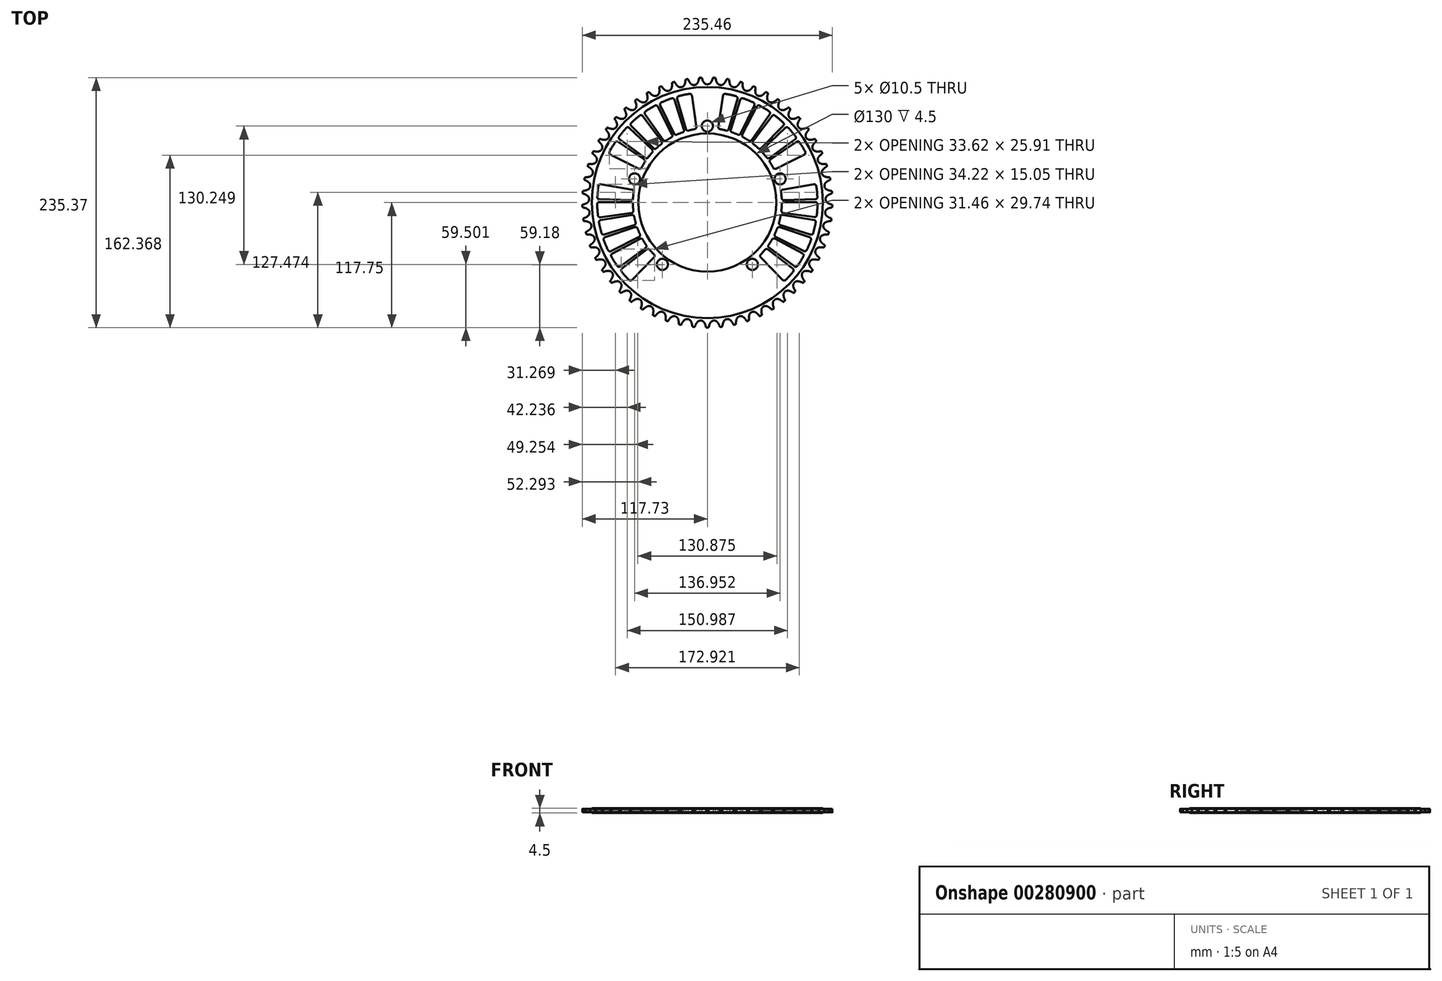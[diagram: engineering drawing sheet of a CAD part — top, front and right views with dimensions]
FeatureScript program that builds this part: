
annotation { "Feature Type Name" : "Feature", "Feature Type Description" : "" }
export const myFeature = defineFeature(function(context is Context, id is Id, definition is map)
    precondition{}
    {
        {
            var Q0;
            Q0=qCreatedBy(makeId("Top.planeOp"),FACE);
            var sketch = newSketch(context, id + "F0", { "sketchPlane" : qUnion([Q0])});
            skCircle(sketch, "E0", {"center": v(0, 0) * mm, "radius": 115.3 * mm, "construction": true});
            skArc(sketch, "E1", {"start": v(-3.25, 112.93) * mm, "mid": v(-1.82, 111.72) * mm, "end": v(0, 111.28) * mm});
            skArc(sketch, "E2", {"start": v(-4.68, 115.65) * mm, "mid": v(-4.07, 114.24) * mm, "end": v(-3.25, 112.93) * mm});
            skLineSegment(sketch, "E3", {"start": v(-4.68, 115.65) * mm, "end": v(-5.07, 116.77) * mm});
            skArc(sketch, "E4", {"start": v(-5.07, 116.77) * mm, "mid": v(-5.69, 118.06) * mm, "end": v(-6.58, 119.19) * mm});
            skArc(sketch, "E5.MirrorCS", {"start": v(3.25, 112.93) * mm, "mid": v(1.82, 111.72) * mm, "end": v(0, 111.28) * mm});
            skArc(sketch, "E6.MirrorCS", {"start": v(4.68, 115.65) * mm, "mid": v(4.07, 114.24) * mm, "end": v(3.25, 112.93) * mm});
            skArc(sketch, "E7.MirrorCS", {"start": v(5.07, 116.77) * mm, "mid": v(5.69, 118.06) * mm, "end": v(6.58, 119.19) * mm});
            skLineSegment(sketch, "E8.MirrorCS", {"start": v(4.68, 115.65) * mm, "end": v(5.07, 116.77) * mm});
            skArc(sketch, "E9.1.0", {"start": v(-17.38, 114.43) * mm, "mid": v(-16.6, 113.1) * mm, "end": v(-15.65, 111.89) * mm});
            skArc(sketch, "E9.1.1", {"start": v(-9.2, 112.6) * mm, "mid": v(-10.48, 111.24) * mm, "end": v(-12.24, 110.6) * mm});
            skArc(sketch, "E9.1.2", {"start": v(-8.07, 115.46) * mm, "mid": v(-8.53, 114) * mm, "end": v(-9.2, 112.6) * mm});
            skArc(sketch, "E9.1.3", {"start": v(-7.8, 116.62) * mm, "mid": v(-7.34, 117.97) * mm, "end": v(-6.58, 119.19) * mm});
            skArc(sketch, "E9.1.4", {"start": v(-17.88, 115.5) * mm, "mid": v(-18.64, 116.72) * mm, "end": v(-19.65, 117.74) * mm});
            skArc(sketch, "E9.1.5", {"start": v(-15.65, 111.89) * mm, "mid": v(-14.1, 110.84) * mm, "end": v(-12.24, 110.6) * mm});
            skLineSegment(sketch, "E9.1.6", {"start": v(-17.38, 114.43) * mm, "end": v(-17.88, 115.5) * mm});
            skLineSegment(sketch, "E9.1.7", {"start": v(-8.07, 115.46) * mm, "end": v(-7.8, 116.62) * mm});
            skArc(sketch, "E9.2.0", {"start": v(-29.86, 111.82) * mm, "mid": v(-28.95, 110.58) * mm, "end": v(-27.86, 109.49) * mm});
            skArc(sketch, "E9.2.1", {"start": v(-21.53, 110.9) * mm, "mid": v(-22.65, 109.41) * mm, "end": v(-24.33, 108.59) * mm});
            skArc(sketch, "E9.2.2", {"start": v(-20.72, 113.87) * mm, "mid": v(-21.01, 112.36) * mm, "end": v(-21.53, 110.9) * mm});
            skArc(sketch, "E9.2.3", {"start": v(-20.59, 115.05) * mm, "mid": v(-20.27, 116.45) * mm, "end": v(-19.65, 117.74) * mm});
            skArc(sketch, "E9.2.4", {"start": v(-30.48, 112.83) * mm, "mid": v(-31.37, 113.96) * mm, "end": v(-32.48, 114.86) * mm});
            skArc(sketch, "E9.2.5", {"start": v(-27.86, 109.49) * mm, "mid": v(-26.2, 108.61) * mm, "end": v(-24.33, 108.59) * mm});
            skLineSegment(sketch, "E9.2.6", {"start": v(-29.86, 111.82) * mm, "end": v(-30.48, 112.83) * mm});
            skLineSegment(sketch, "E9.2.7", {"start": v(-20.72, 113.87) * mm, "end": v(-20.59, 115.05) * mm});
            skArc(sketch, "E9.3.0", {"start": v(-41.98, 107.86) * mm, "mid": v(-40.94, 106.73) * mm, "end": v(-39.74, 105.76) * mm});
            skArc(sketch, "E9.3.1", {"start": v(-33.6, 107.87) * mm, "mid": v(-34.55, 106.25) * mm, "end": v(-36.13, 105.25) * mm});
            skArc(sketch, "E9.3.2", {"start": v(-33.12, 110.9) * mm, "mid": v(-33.25, 109.37) * mm, "end": v(-33.6, 107.87) * mm});
            skArc(sketch, "E9.3.3", {"start": v(-33.12, 112.09) * mm, "mid": v(-32.96, 113.51) * mm, "end": v(-32.48, 114.86) * mm});
            skArc(sketch, "E9.3.4", {"start": v(-42.7, 108.8) * mm, "mid": v(-43.71, 109.82) * mm, "end": v(-44.92, 110.6) * mm});
            skArc(sketch, "E9.3.5", {"start": v(-39.74, 105.76) * mm, "mid": v(-38, 105.07) * mm, "end": v(-36.13, 105.25) * mm});
            skLineSegment(sketch, "E9.3.6", {"start": v(-41.98, 107.86) * mm, "end": v(-42.7, 108.8) * mm});
            skLineSegment(sketch, "E9.3.7", {"start": v(-33.12, 110.9) * mm, "end": v(-33.12, 112.09) * mm});
            skArc(sketch, "E9.4.0", {"start": v(-53.6, 102.59) * mm, "mid": v(-52.43, 101.58) * mm, "end": v(-51.13, 100.75) * mm});
            skArc(sketch, "E9.4.1", {"start": v(-45.26, 103.52) * mm, "mid": v(-46.03, 101.8) * mm, "end": v(-47.5, 100.64) * mm});
            skArc(sketch, "E9.4.2", {"start": v(-45.12, 106.59) * mm, "mid": v(-45.08, 105.05) * mm, "end": v(-45.26, 103.52) * mm});
            skArc(sketch, "E9.4.3", {"start": v(-45.25, 107.76) * mm, "mid": v(-45.24, 109.2) * mm, "end": v(-44.92, 110.6) * mm});
            skArc(sketch, "E9.4.4", {"start": v(-54.42, 103.44) * mm, "mid": v(-55.53, 104.34) * mm, "end": v(-56.81, 104.98) * mm});
            skArc(sketch, "E9.4.5", {"start": v(-51.13, 100.75) * mm, "mid": v(-49.32, 100.25) * mm, "end": v(-47.5, 100.64) * mm});
            skLineSegment(sketch, "E9.4.6", {"start": v(-53.6, 102.59) * mm, "end": v(-54.42, 103.44) * mm});
            skLineSegment(sketch, "E9.4.7", {"start": v(-45.12, 106.59) * mm, "end": v(-45.25, 107.76) * mm});
            skArc(sketch, "E9.5.0", {"start": v(-64.55, 96.07) * mm, "mid": v(-63.29, 95.2) * mm, "end": v(-61.9, 94.5) * mm});
            skArc(sketch, "E9.5.1", {"start": v(-56.37, 97.9) * mm, "mid": v(-56.95, 96.13) * mm, "end": v(-58.27, 94.8) * mm});
            skArc(sketch, "E9.5.2", {"start": v(-56.57, 100.98) * mm, "mid": v(-56.36, 99.45) * mm, "end": v(-56.37, 97.9) * mm});
            skArc(sketch, "E9.5.3", {"start": v(-56.83, 102.13) * mm, "mid": v(-56.98, 103.56) * mm, "end": v(-56.81, 104.98) * mm});
            skArc(sketch, "E9.5.4", {"start": v(-65.47, 96.82) * mm, "mid": v(-66.67, 97.6) * mm, "end": v(-68.02, 98.1) * mm});
            skArc(sketch, "E9.5.5", {"start": v(-61.9, 94.5) * mm, "mid": v(-60.05, 94.22) * mm, "end": v(-58.27, 94.8) * mm});
            skLineSegment(sketch, "E9.5.6", {"start": v(-64.55, 96.07) * mm, "end": v(-65.47, 96.82) * mm});
            skLineSegment(sketch, "E9.5.7", {"start": v(-56.57, 100.98) * mm, "end": v(-56.83, 102.13) * mm});
            skArc(sketch, "E9.6.0", {"start": v(-74.73, 88.39) * mm, "mid": v(-73.37, 87.65) * mm, "end": v(-71.93, 87.13) * mm});
            skArc(sketch, "E9.6.1", {"start": v(-66.8, 91.11) * mm, "mid": v(-67.18, 89.28) * mm, "end": v(-68.35, 87.82) * mm});
            skArc(sketch, "E9.6.2", {"start": v(-67.34, 94.14) * mm, "mid": v(-66.96, 92.65) * mm, "end": v(-66.8, 91.11) * mm});
            skArc(sketch, "E9.6.3", {"start": v(-67.72, 95.26) * mm, "mid": v(-68.03, 96.66) * mm, "end": v(-68.02, 98.1) * mm});
            skArc(sketch, "E9.6.4", {"start": v(-75.72, 89.03) * mm, "mid": v(-77, 89.68) * mm, "end": v(-78.4, 90.02) * mm});
            skArc(sketch, "E9.6.5", {"start": v(-71.93, 87.13) * mm, "mid": v(-70.05, 87.04) * mm, "end": v(-68.35, 87.82) * mm});
            skLineSegment(sketch, "E9.6.6", {"start": v(-74.73, 88.39) * mm, "end": v(-75.72, 89.03) * mm});
            skLineSegment(sketch, "E9.6.7", {"start": v(-67.34, 94.14) * mm, "end": v(-67.72, 95.26) * mm});
            skArc(sketch, "E9.7.0", {"start": v(-84, 79.63) * mm, "mid": v(-82.57, 79.05) * mm, "end": v(-81.07, 78.68) * mm});
            skArc(sketch, "E9.7.1", {"start": v(-76.42, 83.21) * mm, "mid": v(-76.6, 81.35) * mm, "end": v(-77.6, 79.76) * mm});
            skArc(sketch, "E9.7.2", {"start": v(-77.28, 86.16) * mm, "mid": v(-76.74, 84.72) * mm, "end": v(-76.42, 83.21) * mm});
            skArc(sketch, "E9.7.3", {"start": v(-77.79, 87.23) * mm, "mid": v(-78.25, 88.59) * mm, "end": v(-78.4, 90.02) * mm});
            skArc(sketch, "E9.7.4", {"start": v(-85.05, 80.16) * mm, "mid": v(-86.4, 80.66) * mm, "end": v(-87.82, 80.85) * mm});
            skArc(sketch, "E9.7.5", {"start": v(-81.07, 78.68) * mm, "mid": v(-79.2, 78.8) * mm, "end": v(-77.6, 79.76) * mm});
            skLineSegment(sketch, "E9.7.6", {"start": v(-84, 79.63) * mm, "end": v(-85.05, 80.16) * mm});
            skLineSegment(sketch, "E9.7.7", {"start": v(-77.28, 86.16) * mm, "end": v(-77.79, 87.23) * mm});
            skArc(sketch, "E9.8.0", {"start": v(-92.25, 69.9) * mm, "mid": v(-90.77, 69.48) * mm, "end": v(-89.24, 69.29) * mm});
            skArc(sketch, "E9.8.1", {"start": v(-85.11, 74.3) * mm, "mid": v(-85.08, 72.43) * mm, "end": v(-85.9, 70.74) * mm});
            skArc(sketch, "E9.8.2", {"start": v(-86.3, 77.14) * mm, "mid": v(-85.6, 75.76) * mm, "end": v(-85.11, 74.3) * mm});
            skArc(sketch, "E9.8.3", {"start": v(-86.91, 78.14) * mm, "mid": v(-87.52, 79.44) * mm, "end": v(-87.82, 80.85) * mm});
            skArc(sketch, "E9.8.4", {"start": v(-93.36, 70.32) * mm, "mid": v(-94.75, 70.67) * mm, "end": v(-96.18, 70.7) * mm});
            skArc(sketch, "E9.8.5", {"start": v(-89.24, 69.29) * mm, "mid": v(-87.4, 69.61) * mm, "end": v(-85.9, 70.74) * mm});
            skLineSegment(sketch, "E9.8.6", {"start": v(-92.25, 69.9) * mm, "end": v(-93.36, 70.32) * mm});
            skLineSegment(sketch, "E9.8.7", {"start": v(-86.3, 77.14) * mm, "end": v(-86.91, 78.14) * mm});
            skArc(sketch, "E9.9.0", {"start": v(-99.38, 59.33) * mm, "mid": v(-97.86, 59.08) * mm, "end": v(-96.32, 59.05) * mm});
            skArc(sketch, "E9.9.1", {"start": v(-92.77, 64.49) * mm, "mid": v(-92.53, 62.63) * mm, "end": v(-93.16, 60.86) * mm});
            skArc(sketch, "E9.9.2", {"start": v(-94.26, 67.17) * mm, "mid": v(-93.41, 65.88) * mm, "end": v(-92.77, 64.49) * mm});
            skArc(sketch, "E9.9.3", {"start": v(-94.98, 68.1) * mm, "mid": v(-95.73, 69.33) * mm, "end": v(-96.18, 70.7) * mm});
            skArc(sketch, "E9.9.4", {"start": v(-100.53, 59.62) * mm, "mid": v(-101.95, 59.81) * mm, "end": v(-103.38, 59.68) * mm});
            skArc(sketch, "E9.9.5", {"start": v(-96.32, 59.05) * mm, "mid": v(-94.52, 59.58) * mm, "end": v(-93.16, 60.86) * mm});
            skLineSegment(sketch, "E9.9.6", {"start": v(-99.38, 59.33) * mm, "end": v(-100.53, 59.62) * mm});
            skLineSegment(sketch, "E9.9.7", {"start": v(-94.26, 67.17) * mm, "end": v(-94.98, 68.1) * mm});
            skArc(sketch, "E9.10.0", {"start": v(-105.3, 48.04) * mm, "mid": v(-103.76, 47.95) * mm, "end": v(-102.23, 48.1) * mm});
            skArc(sketch, "E9.10.1", {"start": v(-99.3, 53.89) * mm, "mid": v(-98.86, 52.07) * mm, "end": v(-99.29, 50.25) * mm});
            skArc(sketch, "E9.10.2", {"start": v(-101.07, 56.4) * mm, "mid": v(-100.1, 55.2) * mm, "end": v(-99.3, 53.89) * mm});
            skArc(sketch, "E9.10.3", {"start": v(-101.9, 57.25) * mm, "mid": v(-102.77, 58.38) * mm, "end": v(-103.38, 59.68) * mm});
            skArc(sketch, "E9.10.4", {"start": v(-106.47, 48.2) * mm, "mid": v(-107.9, 48.24) * mm, "end": v(-109.31, 47.95) * mm});
            skArc(sketch, "E9.10.5", {"start": v(-102.23, 48.1) * mm, "mid": v(-100.5, 48.82) * mm, "end": v(-99.29, 50.25) * mm});
            skLineSegment(sketch, "E9.10.6", {"start": v(-105.3, 48.04) * mm, "end": v(-106.47, 48.2) * mm});
            skLineSegment(sketch, "E9.10.7", {"start": v(-101.07, 56.4) * mm, "end": v(-101.9, 57.25) * mm});
            skArc(sketch, "E9.11.0", {"start": v(-109.95, 36.16) * mm, "mid": v(-108.4, 36.25) * mm, "end": v(-106.9, 36.56) * mm});
            skArc(sketch, "E9.11.1", {"start": v(-104.62, 42.64) * mm, "mid": v(-103.98, 40.88) * mm, "end": v(-104.21, 39.02) * mm});
            skArc(sketch, "E9.11.2", {"start": v(-106.66, 44.94) * mm, "mid": v(-105.56, 43.86) * mm, "end": v(-104.62, 42.64) * mm});
            skArc(sketch, "E9.11.3", {"start": v(-107.58, 45.69) * mm, "mid": v(-108.57, 46.72) * mm, "end": v(-109.31, 47.95) * mm});
            skArc(sketch, "E9.11.4", {"start": v(-111.13, 36.2) * mm, "mid": v(-112.56, 36.07) * mm, "end": v(-113.93, 35.63) * mm});
            skArc(sketch, "E9.11.5", {"start": v(-106.9, 36.56) * mm, "mid": v(-105.26, 37.47) * mm, "end": v(-104.21, 39.02) * mm});
            skLineSegment(sketch, "E9.11.6", {"start": v(-109.95, 36.16) * mm, "end": v(-111.13, 36.2) * mm});
            skLineSegment(sketch, "E9.11.7", {"start": v(-106.66, 44.94) * mm, "end": v(-107.58, 45.69) * mm});
            skArc(sketch, "E9.12.0", {"start": v(-113.26, 23.85) * mm, "mid": v(-111.74, 24.1) * mm, "end": v(-110.27, 24.58) * mm});
            skArc(sketch, "E9.12.1", {"start": v(-108.68, 30.87) * mm, "mid": v(-107.85, 29.2) * mm, "end": v(-107.87, 27.32) * mm});
            skArc(sketch, "E9.12.2", {"start": v(-110.96, 32.93) * mm, "mid": v(-109.74, 31.98) * mm, "end": v(-108.68, 30.87) * mm});
            skArc(sketch, "E9.12.3", {"start": v(-111.95, 33.58) * mm, "mid": v(-113.05, 34.5) * mm, "end": v(-113.93, 35.63) * mm});
            skArc(sketch, "E9.12.4", {"start": v(-114.44, 23.75) * mm, "mid": v(-115.84, 23.47) * mm, "end": v(-117.15, 22.88) * mm});
            skArc(sketch, "E9.12.5", {"start": v(-110.27, 24.58) * mm, "mid": v(-108.74, 25.66) * mm, "end": v(-107.87, 27.32) * mm});
            skLineSegment(sketch, "E9.12.6", {"start": v(-113.26, 23.85) * mm, "end": v(-114.44, 23.75) * mm});
            skLineSegment(sketch, "E9.12.7", {"start": v(-110.96, 32.93) * mm, "end": v(-111.95, 33.58) * mm});
            skArc(sketch, "E9.13.0", {"start": v(-115.2, 11.25) * mm, "mid": v(-113.71, 11.66) * mm, "end": v(-112.3, 12.3) * mm});
            skArc(sketch, "E9.13.1", {"start": v(-111.42, 18.73) * mm, "mid": v(-110.4, 17.15) * mm, "end": v(-110.22, 15.28) * mm});
            skArc(sketch, "E9.13.2", {"start": v(-113.9, 20.52) * mm, "mid": v(-112.6, 19.72) * mm, "end": v(-111.42, 18.73) * mm});
            skArc(sketch, "E9.13.3", {"start": v(-114.96, 21.06) * mm, "mid": v(-116.16, 21.85) * mm, "end": v(-117.15, 22.88) * mm});
            skArc(sketch, "E9.13.4", {"start": v(-116.36, 11.02) * mm, "mid": v(-117.72, 10.58) * mm, "end": v(-118.96, 9.86) * mm});
            skArc(sketch, "E9.13.5", {"start": v(-112.3, 12.3) * mm, "mid": v(-110.9, 13.54) * mm, "end": v(-110.22, 15.28) * mm});
            skLineSegment(sketch, "E9.13.6", {"start": v(-115.2, 11.25) * mm, "end": v(-116.36, 11.02) * mm});
            skLineSegment(sketch, "E9.13.7", {"start": v(-113.9, 20.52) * mm, "end": v(-114.96, 21.06) * mm});
            skArc(sketch, "E9.14.0", {"start": v(-115.73, -1.5) * mm, "mid": v(-114.3, -0.92) * mm, "end": v(-112.98, -0.13) * mm});
            skArc(sketch, "E9.14.1", {"start": v(-112.8, 6.36) * mm, "mid": v(-111.62, 4.9) * mm, "end": v(-111.24, 3.07) * mm});
            skArc(sketch, "E9.14.2", {"start": v(-115.48, 7.87) * mm, "mid": v(-114.08, 7.21) * mm, "end": v(-112.8, 6.36) * mm});
            skArc(sketch, "E9.14.3", {"start": v(-116.58, 8.28) * mm, "mid": v(-117.86, 8.94) * mm, "end": v(-118.96, 9.86) * mm});
            skArc(sketch, "E9.14.4", {"start": v(-116.86, -1.85) * mm, "mid": v(-118.17, -2.43) * mm, "end": v(-119.32, -3.29) * mm});
            skArc(sketch, "E9.14.5", {"start": v(-112.98, -0.13) * mm, "mid": v(-111.72, 1.26) * mm, "end": v(-111.24, 3.07) * mm});
            skLineSegment(sketch, "E9.14.6", {"start": v(-115.73, -1.5) * mm, "end": v(-116.86, -1.85) * mm});
            skLineSegment(sketch, "E9.14.7", {"start": v(-115.48, 7.87) * mm, "end": v(-116.58, 8.28) * mm});
            skArc(sketch, "E9.15.0", {"start": v(-114.87, -14.22) * mm, "mid": v(-113.51, -13.49) * mm, "end": v(-112.28, -12.56) * mm});
            skArc(sketch, "E9.15.1", {"start": v(-112.81, -6.1) * mm, "mid": v(-111.49, -7.41) * mm, "end": v(-110.9, -9.19) * mm});
            skArc(sketch, "E9.15.2", {"start": v(-115.64, -4.88) * mm, "mid": v(-114.18, -5.38) * mm, "end": v(-112.81, -6.1) * mm});
            skArc(sketch, "E9.15.3", {"start": v(-116.79, -4.6) * mm, "mid": v(-118.13, -4.08) * mm, "end": v(-119.32, -3.29) * mm});
            skArc(sketch, "E9.15.4", {"start": v(-115.95, -14.7) * mm, "mid": v(-117.19, -15.42) * mm, "end": v(-118.24, -16.4) * mm});
            skArc(sketch, "E9.15.5", {"start": v(-112.28, -12.56) * mm, "mid": v(-111.18, -11.04) * mm, "end": v(-110.9, -9.19) * mm});
            skLineSegment(sketch, "E9.15.6", {"start": v(-114.87, -14.22) * mm, "end": v(-115.95, -14.7) * mm});
            skLineSegment(sketch, "E9.15.7", {"start": v(-115.64, -4.88) * mm, "end": v(-116.79, -4.6) * mm});
            skArc(sketch, "E9.16.0", {"start": v(-112.6, -26.77) * mm, "mid": v(-111.34, -25.9) * mm, "end": v(-110.21, -24.84) * mm});
            skArc(sketch, "E9.16.1", {"start": v(-111.46, -18.46) * mm, "mid": v(-110, -19.63) * mm, "end": v(-109.22, -21.33) * mm});
            skArc(sketch, "E9.16.2", {"start": v(-114.4, -17.57) * mm, "mid": v(-112.9, -17.91) * mm, "end": v(-111.46, -18.46) * mm});
            skArc(sketch, "E9.16.3", {"start": v(-115.57, -17.41) * mm, "mid": v(-116.96, -17.05) * mm, "end": v(-118.24, -16.4) * mm});
            skArc(sketch, "E9.16.4", {"start": v(-113.63, -27.36) * mm, "mid": v(-114.78, -28.21) * mm, "end": v(-115.72, -29.3) * mm});
            skArc(sketch, "E9.16.5", {"start": v(-110.21, -24.84) * mm, "mid": v(-109.3, -23.2) * mm, "end": v(-109.22, -21.33) * mm});
            skLineSegment(sketch, "E9.16.6", {"start": v(-112.6, -26.77) * mm, "end": v(-113.63, -27.36) * mm});
            skLineSegment(sketch, "E9.16.7", {"start": v(-114.4, -17.57) * mm, "end": v(-115.57, -17.41) * mm});
            skArc(sketch, "E9.17.0", {"start": v(-108.98, -39) * mm, "mid": v(-107.81, -37.98) * mm, "end": v(-106.81, -36.8) * mm});
            skArc(sketch, "E9.17.1", {"start": v(-108.75, -30.61) * mm, "mid": v(-107.17, -31.61) * mm, "end": v(-106.2, -33.22) * mm});
            skArc(sketch, "E9.17.2", {"start": v(-111.77, -30.05) * mm, "mid": v(-110.24, -30.22) * mm, "end": v(-108.75, -30.61) * mm});
            skArc(sketch, "E9.17.3", {"start": v(-112.96, -30.02) * mm, "mid": v(-114.38, -29.82) * mm, "end": v(-115.72, -29.3) * mm});
            skArc(sketch, "E9.17.4", {"start": v(-109.93, -39.7) * mm, "mid": v(-110.98, -40.67) * mm, "end": v(-111.79, -41.85) * mm});
            skArc(sketch, "E9.17.5", {"start": v(-106.81, -36.8) * mm, "mid": v(-106.08, -35.09) * mm, "end": v(-106.2, -33.22) * mm});
            skLineSegment(sketch, "E9.17.6", {"start": v(-108.98, -39) * mm, "end": v(-109.93, -39.7) * mm});
            skLineSegment(sketch, "E9.17.7", {"start": v(-111.77, -30.05) * mm, "end": v(-112.96, -30.02) * mm});
            skArc(sketch, "E9.18.0", {"start": v(-104.03, -50.74) * mm, "mid": v(-102.98, -49.61) * mm, "end": v(-102.12, -48.34) * mm});
            skArc(sketch, "E9.18.1", {"start": v(-104.72, -42.4) * mm, "mid": v(-103.04, -43.2) * mm, "end": v(-101.9, -44.7) * mm});
            skArc(sketch, "E9.18.2", {"start": v(-107.79, -42.17) * mm, "mid": v(-106.25, -42.17) * mm, "end": v(-104.72, -42.4) * mm});
            skArc(sketch, "E9.18.3", {"start": v(-108.97, -42.26) * mm, "mid": v(-110.4, -42.22) * mm, "end": v(-111.79, -41.85) * mm});
            skArc(sketch, "E9.18.4", {"start": v(-104.9, -51.55) * mm, "mid": v(-105.83, -52.63) * mm, "end": v(-106.5, -53.9) * mm});
            skArc(sketch, "E9.18.5", {"start": v(-102.12, -48.34) * mm, "mid": v(-101.58, -46.54) * mm, "end": v(-101.9, -44.7) * mm});
            skLineSegment(sketch, "E9.18.6", {"start": v(-104.03, -50.74) * mm, "end": v(-104.9, -51.55) * mm});
            skLineSegment(sketch, "E9.18.7", {"start": v(-107.79, -42.17) * mm, "end": v(-108.97, -42.26) * mm});
            skArc(sketch, "E9.19.0", {"start": v(-97.81, -61.88) * mm, "mid": v(-96.9, -60.64) * mm, "end": v(-96.18, -59.28) * mm});
            skArc(sketch, "E9.19.1", {"start": v(-99.42, -53.65) * mm, "mid": v(-97.66, -54.28) * mm, "end": v(-96.37, -55.64) * mm});
            skArc(sketch, "E9.19.2", {"start": v(-102.5, -53.77) * mm, "mid": v(-100.96, -53.6) * mm, "end": v(-99.42, -53.65) * mm});
            skArc(sketch, "E9.19.3", {"start": v(-103.66, -54) * mm, "mid": v(-105.09, -54.1) * mm, "end": v(-106.5, -53.9) * mm});
            skArc(sketch, "E9.19.4", {"start": v(-98.59, -62.77) * mm, "mid": v(-99.4, -63.95) * mm, "end": v(-99.93, -65.29) * mm});
            skArc(sketch, "E9.19.5", {"start": v(-96.18, -59.28) * mm, "mid": v(-95.84, -57.44) * mm, "end": v(-96.37, -55.64) * mm});
            skLineSegment(sketch, "E9.19.6", {"start": v(-97.81, -61.88) * mm, "end": v(-98.59, -62.77) * mm});
            skLineSegment(sketch, "E9.19.7", {"start": v(-102.5, -53.77) * mm, "end": v(-103.66, -54) * mm});
            skArc(sketch, "E9.20.0", {"start": v(-90.41, -72.26) * mm, "mid": v(-89.64, -70.93) * mm, "end": v(-89.07, -69.5) * mm});
            skArc(sketch, "E9.20.1", {"start": v(-92.92, -64.27) * mm, "mid": v(-91.1, -64.7) * mm, "end": v(-89.67, -65.9) * mm});
            skArc(sketch, "E9.20.2", {"start": v(-95.96, -64.72) * mm, "mid": v(-94.46, -64.38) * mm, "end": v(-92.92, -64.27) * mm});
            skArc(sketch, "E9.20.3", {"start": v(-97.09, -65.07) * mm, "mid": v(-98.5, -65.34) * mm, "end": v(-99.93, -65.29) * mm});
            skArc(sketch, "E9.20.4", {"start": v(-91.08, -73.24) * mm, "mid": v(-91.76, -74.5) * mm, "end": v(-92.14, -75.88) * mm});
            skArc(sketch, "E9.20.5", {"start": v(-89.07, -69.5) * mm, "mid": v(-88.94, -67.63) * mm, "end": v(-89.67, -65.9) * mm});
            skLineSegment(sketch, "E9.20.6", {"start": v(-90.41, -72.26) * mm, "end": v(-91.08, -73.24) * mm});
            skLineSegment(sketch, "E9.20.7", {"start": v(-95.96, -64.72) * mm, "end": v(-97.09, -65.07) * mm});
            skArc(sketch, "E9.21.0", {"start": v(-81.91, -81.77) * mm, "mid": v(-81.3, -80.36) * mm, "end": v(-80.89, -78.87) * mm});
            skArc(sketch, "E9.21.1", {"start": v(-85.29, -74.1) * mm, "mid": v(-83.43, -74.32) * mm, "end": v(-81.87, -75.37) * mm});
            skArc(sketch, "E9.21.2", {"start": v(-88.26, -74.88) * mm, "mid": v(-86.8, -74.38) * mm, "end": v(-85.29, -74.1) * mm});
            skArc(sketch, "E9.21.3", {"start": v(-89.34, -75.35) * mm, "mid": v(-90.71, -75.78) * mm, "end": v(-92.14, -75.88) * mm});
            skArc(sketch, "E9.21.4", {"start": v(-82.48, -82.81) * mm, "mid": v(-83, -84.14) * mm, "end": v(-83.23, -85.56) * mm});
            skArc(sketch, "E9.21.5", {"start": v(-80.89, -78.87) * mm, "mid": v(-80.96, -77) * mm, "end": v(-81.87, -75.37) * mm});
            skLineSegment(sketch, "E9.21.6", {"start": v(-81.91, -81.77) * mm, "end": v(-82.48, -82.81) * mm});
            skLineSegment(sketch, "E9.21.7", {"start": v(-88.26, -74.88) * mm, "end": v(-89.34, -75.35) * mm});
            skArc(sketch, "E9.22.0", {"start": v(-72.42, -90.29) * mm, "mid": v(-71.96, -88.82) * mm, "end": v(-71.72, -87.3) * mm});
            skArc(sketch, "E9.22.1", {"start": v(-76.62, -83.03) * mm, "mid": v(-74.74, -83.05) * mm, "end": v(-73.08, -83.92) * mm});
            skArc(sketch, "E9.22.2", {"start": v(-79.48, -84.14) * mm, "mid": v(-78.1, -83.48) * mm, "end": v(-76.62, -83.03) * mm});
            skArc(sketch, "E9.22.3", {"start": v(-80.5, -84.73) * mm, "mid": v(-81.82, -85.3) * mm, "end": v(-83.23, -85.56) * mm});
            skArc(sketch, "E9.22.4", {"start": v(-72.86, -91.38) * mm, "mid": v(-73.25, -92.77) * mm, "end": v(-73.32, -94.2) * mm});
            skArc(sketch, "E9.22.5", {"start": v(-71.72, -87.3) * mm, "mid": v(-72, -85.44) * mm, "end": v(-73.08, -83.92) * mm});
            skLineSegment(sketch, "E9.22.6", {"start": v(-72.42, -90.29) * mm, "end": v(-72.86, -91.38) * mm});
            skLineSegment(sketch, "E9.22.7", {"start": v(-79.48, -84.14) * mm, "end": v(-80.5, -84.73) * mm});
            skArc(sketch, "E9.23.0", {"start": v(-62.05, -97.7) * mm, "mid": v(-61.75, -96.2) * mm, "end": v(-61.68, -94.65) * mm});
            skArc(sketch, "E9.23.1", {"start": v(-67.02, -90.95) * mm, "mid": v(-65.15, -90.77) * mm, "end": v(-63.4, -91.45) * mm});
            skArc(sketch, "E9.23.2", {"start": v(-69.75, -92.37) * mm, "mid": v(-68.43, -91.56) * mm, "end": v(-67.02, -90.95) * mm});
            skArc(sketch, "E9.23.3", {"start": v(-70.7, -93.07) * mm, "mid": v(-71.94, -93.78) * mm, "end": v(-73.32, -94.2) * mm});
            skArc(sketch, "E9.23.4", {"start": v(-62.37, -98.84) * mm, "mid": v(-62.6, -100.26) * mm, "end": v(-62.5, -101.7) * mm});
            skArc(sketch, "E9.23.5", {"start": v(-61.68, -94.65) * mm, "mid": v(-62.16, -92.84) * mm, "end": v(-63.4, -91.45) * mm});
            skLineSegment(sketch, "E9.23.6", {"start": v(-62.05, -97.7) * mm, "end": v(-62.37, -98.84) * mm});
            skLineSegment(sketch, "E9.23.7", {"start": v(-69.75, -92.37) * mm, "end": v(-70.7, -93.07) * mm});
            skArc(sketch, "E9.24.0", {"start": v(-50.92, -103.94) * mm, "mid": v(-50.8, -102.4) * mm, "end": v(-50.9, -100.87) * mm});
            skArc(sketch, "E9.24.1", {"start": v(-56.6, -97.78) * mm, "mid": v(-54.77, -97.38) * mm, "end": v(-52.96, -97.87) * mm});
            skArc(sketch, "E9.24.2", {"start": v(-59.16, -99.48) * mm, "mid": v(-57.95, -98.53) * mm, "end": v(-56.6, -97.78) * mm});
            skArc(sketch, "E9.24.3", {"start": v(-60.03, -100.28) * mm, "mid": v(-61.2, -101.13) * mm, "end": v(-62.5, -101.7) * mm});
            skArc(sketch, "E9.24.4", {"start": v(-51.12, -105.1) * mm, "mid": v(-51.2, -106.54) * mm, "end": v(-50.94, -107.95) * mm});
            skArc(sketch, "E9.24.5", {"start": v(-50.9, -100.87) * mm, "mid": v(-51.57, -99.12) * mm, "end": v(-52.96, -97.87) * mm});
            skLineSegment(sketch, "E9.24.6", {"start": v(-50.92, -103.94) * mm, "end": v(-51.12, -105.1) * mm});
            skLineSegment(sketch, "E9.24.7", {"start": v(-59.16, -99.48) * mm, "end": v(-60.03, -100.28) * mm});
            skArc(sketch, "E9.25.0", {"start": v(-39.18, -108.9) * mm, "mid": v(-39.22, -107.37) * mm, "end": v(-39.49, -105.85) * mm});
            skArc(sketch, "E9.25.1", {"start": v(-45.5, -103.4) * mm, "mid": v(-43.73, -102.82) * mm, "end": v(-41.88, -103.1) * mm});
            skArc(sketch, "E9.25.2", {"start": v(-47.86, -105.39) * mm, "mid": v(-46.75, -104.3) * mm, "end": v(-45.5, -103.4) * mm});
            skArc(sketch, "E9.25.3", {"start": v(-48.64, -106.28) * mm, "mid": v(-49.7, -107.24) * mm, "end": v(-50.94, -107.95) * mm});
            skArc(sketch, "E9.25.4", {"start": v(-39.24, -110.1) * mm, "mid": v(-39.16, -111.52) * mm, "end": v(-38.76, -112.9) * mm});
            skArc(sketch, "E9.25.5", {"start": v(-39.49, -105.85) * mm, "mid": v(-40.35, -104.19) * mm, "end": v(-41.88, -103.1) * mm});
            skLineSegment(sketch, "E9.25.6", {"start": v(-39.18, -108.9) * mm, "end": v(-39.24, -110.1) * mm});
            skLineSegment(sketch, "E9.25.7", {"start": v(-47.86, -105.39) * mm, "end": v(-48.64, -106.28) * mm});
            skArc(sketch, "E9.26.0", {"start": v(-26.96, -112.56) * mm, "mid": v(-27.17, -111.03) * mm, "end": v(-27.6, -109.55) * mm});
            skArc(sketch, "E9.26.1", {"start": v(-33.85, -107.79) * mm, "mid": v(-32.15, -107) * mm, "end": v(-30.28, -107.08) * mm});
            skArc(sketch, "E9.26.2", {"start": v(-35.97, -110.01) * mm, "mid": v(-35, -108.82) * mm, "end": v(-33.85, -107.79) * mm});
            skArc(sketch, "E9.26.3", {"start": v(-36.65, -110.98) * mm, "mid": v(-37.6, -112.06) * mm, "end": v(-38.76, -112.9) * mm});
            skArc(sketch, "E9.26.4", {"start": v(-26.9, -113.74) * mm, "mid": v(-26.65, -115.15) * mm, "end": v(-26.1, -116.48) * mm});
            skArc(sketch, "E9.26.5", {"start": v(-27.6, -109.55) * mm, "mid": v(-28.65, -108) * mm, "end": v(-30.28, -107.08) * mm});
            skLineSegment(sketch, "E9.26.6", {"start": v(-26.96, -112.56) * mm, "end": v(-26.9, -113.74) * mm});
            skLineSegment(sketch, "E9.26.7", {"start": v(-35.97, -110.01) * mm, "end": v(-36.65, -110.98) * mm});
            skArc(sketch, "E9.27.0", {"start": v(-14.42, -114.84) * mm, "mid": v(-14.8, -113.35) * mm, "end": v(-15.39, -111.93) * mm});
            skArc(sketch, "E9.27.1", {"start": v(-21.79, -110.86) * mm, "mid": v(-20.18, -109.9) * mm, "end": v(-18.32, -109.76) * mm});
            skArc(sketch, "E9.27.2", {"start": v(-23.65, -113.3) * mm, "mid": v(-22.81, -112) * mm, "end": v(-21.79, -110.86) * mm});
            skArc(sketch, "E9.27.3", {"start": v(-24.22, -114.34) * mm, "mid": v(-25.04, -115.52) * mm, "end": v(-26.1, -116.48) * mm});
            skArc(sketch, "E9.27.4", {"start": v(-14.22, -116) * mm, "mid": v(-13.82, -117.39) * mm, "end": v(-13.13, -118.64) * mm});
            skArc(sketch, "E9.27.5", {"start": v(-15.39, -111.93) * mm, "mid": v(-16.6, -110.5) * mm, "end": v(-18.32, -109.76) * mm});
            skLineSegment(sketch, "E9.27.6", {"start": v(-14.42, -114.84) * mm, "end": v(-14.22, -116) * mm});
            skLineSegment(sketch, "E9.27.7", {"start": v(-23.65, -113.3) * mm, "end": v(-24.22, -114.34) * mm});
            skArc(sketch, "E9.28.0", {"start": v(-1.7, -115.73) * mm, "mid": v(-2.23, -114.29) * mm, "end": v(-2.98, -112.94) * mm});
            skArc(sketch, "E9.28.1", {"start": v(-9.46, -112.58) * mm, "mid": v(-7.97, -111.45) * mm, "end": v(-6.13, -111.11) * mm});
            skArc(sketch, "E9.28.2", {"start": v(-11.05, -115.21) * mm, "mid": v(-10.35, -113.84) * mm, "end": v(-9.46, -112.58) * mm});
            skArc(sketch, "E9.28.3", {"start": v(-11.5, -116.31) * mm, "mid": v(-12.18, -117.57) * mm, "end": v(-13.13, -118.64) * mm});
            skArc(sketch, "E9.28.4", {"start": v(-1.37, -116.87) * mm, "mid": v(-0.83, -118.2) * mm, "end": v(0, -119.37) * mm});
            skArc(sketch, "E9.28.5", {"start": v(-2.98, -112.94) * mm, "mid": v(-4.34, -111.65) * mm, "end": v(-6.13, -111.11) * mm});
            skLineSegment(sketch, "E9.28.6", {"start": v(-1.7, -115.73) * mm, "end": v(-1.37, -116.87) * mm});
            skLineSegment(sketch, "E9.28.7", {"start": v(-11.05, -115.21) * mm, "end": v(-11.5, -116.31) * mm});
            skArc(sketch, "E9.29.0", {"start": v(11.05, -115.21) * mm, "mid": v(10.35, -113.84) * mm, "end": v(9.46, -112.58) * mm});
            skArc(sketch, "E9.29.1", {"start": v(2.98, -112.94) * mm, "mid": v(4.34, -111.65) * mm, "end": v(6.13, -111.11) * mm});
            skArc(sketch, "E9.29.2", {"start": v(1.7, -115.73) * mm, "mid": v(2.23, -114.29) * mm, "end": v(2.98, -112.94) * mm});
            skArc(sketch, "E9.29.3", {"start": v(1.37, -116.87) * mm, "mid": v(0.83, -118.2) * mm, "end": v(0, -119.37) * mm});
            skArc(sketch, "E9.29.4", {"start": v(11.5, -116.31) * mm, "mid": v(12.18, -117.57) * mm, "end": v(13.13, -118.64) * mm});
            skArc(sketch, "E9.29.5", {"start": v(9.46, -112.58) * mm, "mid": v(7.97, -111.45) * mm, "end": v(6.13, -111.11) * mm});
            skLineSegment(sketch, "E9.29.6", {"start": v(11.05, -115.21) * mm, "end": v(11.5, -116.31) * mm});
            skLineSegment(sketch, "E9.29.7", {"start": v(1.7, -115.73) * mm, "end": v(1.37, -116.87) * mm});
            skArc(sketch, "E9.30.0", {"start": v(23.65, -113.3) * mm, "mid": v(22.81, -112) * mm, "end": v(21.79, -110.86) * mm});
            skArc(sketch, "E9.30.1", {"start": v(15.39, -111.93) * mm, "mid": v(16.6, -110.5) * mm, "end": v(18.32, -109.76) * mm});
            skArc(sketch, "E9.30.2", {"start": v(14.42, -114.84) * mm, "mid": v(14.8, -113.35) * mm, "end": v(15.39, -111.93) * mm});
            skArc(sketch, "E9.30.3", {"start": v(14.22, -116) * mm, "mid": v(13.82, -117.39) * mm, "end": v(13.13, -118.64) * mm});
            skArc(sketch, "E9.30.4", {"start": v(24.22, -114.34) * mm, "mid": v(25.04, -115.52) * mm, "end": v(26.1, -116.48) * mm});
            skArc(sketch, "E9.30.5", {"start": v(21.79, -110.86) * mm, "mid": v(20.18, -109.9) * mm, "end": v(18.32, -109.76) * mm});
            skLineSegment(sketch, "E9.30.6", {"start": v(23.65, -113.3) * mm, "end": v(24.22, -114.34) * mm});
            skLineSegment(sketch, "E9.30.7", {"start": v(14.42, -114.84) * mm, "end": v(14.22, -116) * mm});
            skArc(sketch, "E9.31.0", {"start": v(35.97, -110.01) * mm, "mid": v(35, -108.82) * mm, "end": v(33.85, -107.79) * mm});
            skArc(sketch, "E9.31.1", {"start": v(27.6, -109.55) * mm, "mid": v(28.65, -108) * mm, "end": v(30.28, -107.08) * mm});
            skArc(sketch, "E9.31.2", {"start": v(26.96, -112.56) * mm, "mid": v(27.17, -111.03) * mm, "end": v(27.6, -109.55) * mm});
            skArc(sketch, "E9.31.3", {"start": v(26.9, -113.74) * mm, "mid": v(26.65, -115.15) * mm, "end": v(26.1, -116.48) * mm});
            skArc(sketch, "E9.31.4", {"start": v(36.65, -110.98) * mm, "mid": v(37.6, -112.06) * mm, "end": v(38.76, -112.9) * mm});
            skArc(sketch, "E9.31.5", {"start": v(33.85, -107.79) * mm, "mid": v(32.15, -107) * mm, "end": v(30.28, -107.08) * mm});
            skLineSegment(sketch, "E9.31.6", {"start": v(35.97, -110.01) * mm, "end": v(36.65, -110.98) * mm});
            skLineSegment(sketch, "E9.31.7", {"start": v(26.96, -112.56) * mm, "end": v(26.9, -113.74) * mm});
            skArc(sketch, "E9.32.0", {"start": v(47.86, -105.39) * mm, "mid": v(46.75, -104.3) * mm, "end": v(45.5, -103.4) * mm});
            skArc(sketch, "E9.32.1", {"start": v(39.49, -105.85) * mm, "mid": v(40.35, -104.19) * mm, "end": v(41.88, -103.1) * mm});
            skArc(sketch, "E9.32.2", {"start": v(39.18, -108.9) * mm, "mid": v(39.22, -107.37) * mm, "end": v(39.49, -105.85) * mm});
            skArc(sketch, "E9.32.3", {"start": v(39.24, -110.1) * mm, "mid": v(39.16, -111.52) * mm, "end": v(38.76, -112.9) * mm});
            skArc(sketch, "E9.32.4", {"start": v(48.64, -106.28) * mm, "mid": v(49.7, -107.24) * mm, "end": v(50.94, -107.95) * mm});
            skArc(sketch, "E9.32.5", {"start": v(45.5, -103.4) * mm, "mid": v(43.73, -102.82) * mm, "end": v(41.88, -103.1) * mm});
            skLineSegment(sketch, "E9.32.6", {"start": v(47.86, -105.39) * mm, "end": v(48.64, -106.28) * mm});
            skLineSegment(sketch, "E9.32.7", {"start": v(39.18, -108.9) * mm, "end": v(39.24, -110.1) * mm});
            skArc(sketch, "E9.33.0", {"start": v(59.16, -99.48) * mm, "mid": v(57.95, -98.53) * mm, "end": v(56.6, -97.78) * mm});
            skArc(sketch, "E9.33.1", {"start": v(50.9, -100.87) * mm, "mid": v(51.57, -99.12) * mm, "end": v(52.96, -97.87) * mm});
            skArc(sketch, "E9.33.2", {"start": v(50.92, -103.94) * mm, "mid": v(50.8, -102.4) * mm, "end": v(50.9, -100.87) * mm});
            skArc(sketch, "E9.33.3", {"start": v(51.12, -105.1) * mm, "mid": v(51.2, -106.54) * mm, "end": v(50.94, -107.95) * mm});
            skArc(sketch, "E9.33.4", {"start": v(60.03, -100.28) * mm, "mid": v(61.2, -101.13) * mm, "end": v(62.5, -101.7) * mm});
            skArc(sketch, "E9.33.5", {"start": v(56.6, -97.78) * mm, "mid": v(54.77, -97.38) * mm, "end": v(52.96, -97.87) * mm});
            skLineSegment(sketch, "E9.33.6", {"start": v(59.16, -99.48) * mm, "end": v(60.03, -100.28) * mm});
            skLineSegment(sketch, "E9.33.7", {"start": v(50.92, -103.94) * mm, "end": v(51.12, -105.1) * mm});
            skArc(sketch, "E9.34.0", {"start": v(69.75, -92.37) * mm, "mid": v(68.43, -91.56) * mm, "end": v(67.02, -90.95) * mm});
            skArc(sketch, "E9.34.1", {"start": v(61.68, -94.65) * mm, "mid": v(62.16, -92.84) * mm, "end": v(63.4, -91.45) * mm});
            skArc(sketch, "E9.34.2", {"start": v(62.05, -97.7) * mm, "mid": v(61.75, -96.2) * mm, "end": v(61.68, -94.65) * mm});
            skArc(sketch, "E9.34.3", {"start": v(62.37, -98.84) * mm, "mid": v(62.6, -100.26) * mm, "end": v(62.5, -101.7) * mm});
            skArc(sketch, "E9.34.4", {"start": v(70.7, -93.07) * mm, "mid": v(71.94, -93.78) * mm, "end": v(73.32, -94.2) * mm});
            skArc(sketch, "E9.34.5", {"start": v(67.02, -90.95) * mm, "mid": v(65.15, -90.77) * mm, "end": v(63.4, -91.45) * mm});
            skLineSegment(sketch, "E9.34.6", {"start": v(69.75, -92.37) * mm, "end": v(70.7, -93.07) * mm});
            skLineSegment(sketch, "E9.34.7", {"start": v(62.05, -97.7) * mm, "end": v(62.37, -98.84) * mm});
            skArc(sketch, "E9.35.0", {"start": v(79.48, -84.14) * mm, "mid": v(78.1, -83.48) * mm, "end": v(76.62, -83.03) * mm});
            skArc(sketch, "E9.35.1", {"start": v(71.72, -87.3) * mm, "mid": v(72, -85.44) * mm, "end": v(73.08, -83.92) * mm});
            skArc(sketch, "E9.35.2", {"start": v(72.42, -90.29) * mm, "mid": v(71.96, -88.82) * mm, "end": v(71.72, -87.3) * mm});
            skArc(sketch, "E9.35.3", {"start": v(72.86, -91.38) * mm, "mid": v(73.25, -92.77) * mm, "end": v(73.32, -94.2) * mm});
            skArc(sketch, "E9.35.4", {"start": v(80.5, -84.73) * mm, "mid": v(81.82, -85.3) * mm, "end": v(83.23, -85.56) * mm});
            skArc(sketch, "E9.35.5", {"start": v(76.62, -83.03) * mm, "mid": v(74.74, -83.05) * mm, "end": v(73.08, -83.92) * mm});
            skLineSegment(sketch, "E9.35.6", {"start": v(79.48, -84.14) * mm, "end": v(80.5, -84.73) * mm});
            skLineSegment(sketch, "E9.35.7", {"start": v(72.42, -90.29) * mm, "end": v(72.86, -91.38) * mm});
            skArc(sketch, "E9.36.0", {"start": v(88.26, -74.88) * mm, "mid": v(86.8, -74.38) * mm, "end": v(85.29, -74.1) * mm});
            skArc(sketch, "E9.36.1", {"start": v(80.89, -78.87) * mm, "mid": v(80.96, -77) * mm, "end": v(81.87, -75.37) * mm});
            skArc(sketch, "E9.36.2", {"start": v(81.91, -81.77) * mm, "mid": v(81.3, -80.36) * mm, "end": v(80.89, -78.87) * mm});
            skArc(sketch, "E9.36.3", {"start": v(82.48, -82.81) * mm, "mid": v(83, -84.14) * mm, "end": v(83.23, -85.56) * mm});
            skArc(sketch, "E9.36.4", {"start": v(89.34, -75.35) * mm, "mid": v(90.71, -75.78) * mm, "end": v(92.14, -75.88) * mm});
            skArc(sketch, "E9.36.5", {"start": v(85.29, -74.1) * mm, "mid": v(83.43, -74.32) * mm, "end": v(81.87, -75.37) * mm});
            skLineSegment(sketch, "E9.36.6", {"start": v(88.26, -74.88) * mm, "end": v(89.34, -75.35) * mm});
            skLineSegment(sketch, "E9.36.7", {"start": v(81.91, -81.77) * mm, "end": v(82.48, -82.81) * mm});
            skArc(sketch, "E9.37.0", {"start": v(95.96, -64.72) * mm, "mid": v(94.46, -64.38) * mm, "end": v(92.92, -64.27) * mm});
            skArc(sketch, "E9.37.1", {"start": v(89.07, -69.5) * mm, "mid": v(88.94, -67.63) * mm, "end": v(89.67, -65.9) * mm});
            skArc(sketch, "E9.37.2", {"start": v(90.41, -72.26) * mm, "mid": v(89.64, -70.93) * mm, "end": v(89.07, -69.5) * mm});
            skArc(sketch, "E9.37.3", {"start": v(91.08, -73.24) * mm, "mid": v(91.76, -74.5) * mm, "end": v(92.14, -75.88) * mm});
            skArc(sketch, "E9.37.4", {"start": v(97.09, -65.07) * mm, "mid": v(98.5, -65.34) * mm, "end": v(99.93, -65.29) * mm});
            skArc(sketch, "E9.37.5", {"start": v(92.92, -64.27) * mm, "mid": v(91.1, -64.7) * mm, "end": v(89.67, -65.9) * mm});
            skLineSegment(sketch, "E9.37.6", {"start": v(95.96, -64.72) * mm, "end": v(97.09, -65.07) * mm});
            skLineSegment(sketch, "E9.37.7", {"start": v(90.41, -72.26) * mm, "end": v(91.08, -73.24) * mm});
            skArc(sketch, "E9.38.0", {"start": v(102.5, -53.77) * mm, "mid": v(100.96, -53.6) * mm, "end": v(99.42, -53.65) * mm});
            skArc(sketch, "E9.38.1", {"start": v(96.18, -59.28) * mm, "mid": v(95.84, -57.44) * mm, "end": v(96.37, -55.64) * mm});
            skArc(sketch, "E9.38.2", {"start": v(97.81, -61.88) * mm, "mid": v(96.9, -60.64) * mm, "end": v(96.18, -59.28) * mm});
            skArc(sketch, "E9.38.3", {"start": v(98.59, -62.77) * mm, "mid": v(99.4, -63.95) * mm, "end": v(99.93, -65.29) * mm});
            skArc(sketch, "E9.38.4", {"start": v(103.66, -54) * mm, "mid": v(105.09, -54.1) * mm, "end": v(106.5, -53.9) * mm});
            skArc(sketch, "E9.38.5", {"start": v(99.42, -53.65) * mm, "mid": v(97.66, -54.28) * mm, "end": v(96.37, -55.64) * mm});
            skLineSegment(sketch, "E9.38.6", {"start": v(102.5, -53.77) * mm, "end": v(103.66, -54) * mm});
            skLineSegment(sketch, "E9.38.7", {"start": v(97.81, -61.88) * mm, "end": v(98.59, -62.77) * mm});
            skArc(sketch, "E9.39.0", {"start": v(107.79, -42.17) * mm, "mid": v(106.25, -42.17) * mm, "end": v(104.72, -42.4) * mm});
            skArc(sketch, "E9.39.1", {"start": v(102.12, -48.34) * mm, "mid": v(101.58, -46.54) * mm, "end": v(101.9, -44.7) * mm});
            skArc(sketch, "E9.39.2", {"start": v(104.03, -50.74) * mm, "mid": v(102.98, -49.61) * mm, "end": v(102.12, -48.34) * mm});
            skArc(sketch, "E9.39.3", {"start": v(104.9, -51.55) * mm, "mid": v(105.83, -52.63) * mm, "end": v(106.5, -53.9) * mm});
            skArc(sketch, "E9.39.4", {"start": v(108.97, -42.26) * mm, "mid": v(110.4, -42.22) * mm, "end": v(111.79, -41.85) * mm});
            skArc(sketch, "E9.39.5", {"start": v(104.72, -42.4) * mm, "mid": v(103.04, -43.2) * mm, "end": v(101.9, -44.7) * mm});
            skLineSegment(sketch, "E9.39.6", {"start": v(107.79, -42.17) * mm, "end": v(108.97, -42.26) * mm});
            skLineSegment(sketch, "E9.39.7", {"start": v(104.03, -50.74) * mm, "end": v(104.9, -51.55) * mm});
            skArc(sketch, "E9.40.0", {"start": v(111.77, -30.05) * mm, "mid": v(110.24, -30.22) * mm, "end": v(108.75, -30.61) * mm});
            skArc(sketch, "E9.40.1", {"start": v(106.81, -36.8) * mm, "mid": v(106.08, -35.09) * mm, "end": v(106.2, -33.22) * mm});
            skArc(sketch, "E9.40.2", {"start": v(108.98, -39) * mm, "mid": v(107.81, -37.98) * mm, "end": v(106.81, -36.8) * mm});
            skArc(sketch, "E9.40.3", {"start": v(109.93, -39.7) * mm, "mid": v(110.98, -40.67) * mm, "end": v(111.79, -41.85) * mm});
            skArc(sketch, "E9.40.4", {"start": v(112.96, -30.02) * mm, "mid": v(114.38, -29.82) * mm, "end": v(115.72, -29.3) * mm});
            skArc(sketch, "E9.40.5", {"start": v(108.75, -30.61) * mm, "mid": v(107.17, -31.61) * mm, "end": v(106.2, -33.22) * mm});
            skLineSegment(sketch, "E9.40.6", {"start": v(111.77, -30.05) * mm, "end": v(112.96, -30.02) * mm});
            skLineSegment(sketch, "E9.40.7", {"start": v(108.98, -39) * mm, "end": v(109.93, -39.7) * mm});
            skArc(sketch, "E9.41.0", {"start": v(114.4, -17.57) * mm, "mid": v(112.9, -17.91) * mm, "end": v(111.46, -18.46) * mm});
            skArc(sketch, "E9.41.1", {"start": v(110.21, -24.84) * mm, "mid": v(109.3, -23.2) * mm, "end": v(109.22, -21.33) * mm});
            skArc(sketch, "E9.41.2", {"start": v(112.6, -26.77) * mm, "mid": v(111.34, -25.9) * mm, "end": v(110.21, -24.84) * mm});
            skArc(sketch, "E9.41.3", {"start": v(113.63, -27.36) * mm, "mid": v(114.78, -28.21) * mm, "end": v(115.72, -29.3) * mm});
            skArc(sketch, "E9.41.4", {"start": v(115.57, -17.41) * mm, "mid": v(116.96, -17.05) * mm, "end": v(118.24, -16.4) * mm});
            skArc(sketch, "E9.41.5", {"start": v(111.46, -18.46) * mm, "mid": v(110, -19.63) * mm, "end": v(109.22, -21.33) * mm});
            skLineSegment(sketch, "E9.41.6", {"start": v(114.4, -17.57) * mm, "end": v(115.57, -17.41) * mm});
            skLineSegment(sketch, "E9.41.7", {"start": v(112.6, -26.77) * mm, "end": v(113.63, -27.36) * mm});
            skArc(sketch, "E9.42.0", {"start": v(115.64, -4.88) * mm, "mid": v(114.18, -5.38) * mm, "end": v(112.81, -6.1) * mm});
            skArc(sketch, "E9.42.1", {"start": v(112.28, -12.56) * mm, "mid": v(111.18, -11.04) * mm, "end": v(110.9, -9.19) * mm});
            skArc(sketch, "E9.42.2", {"start": v(114.87, -14.22) * mm, "mid": v(113.51, -13.49) * mm, "end": v(112.28, -12.56) * mm});
            skArc(sketch, "E9.42.3", {"start": v(115.95, -14.7) * mm, "mid": v(117.19, -15.42) * mm, "end": v(118.24, -16.4) * mm});
            skArc(sketch, "E9.42.4", {"start": v(116.79, -4.6) * mm, "mid": v(118.13, -4.08) * mm, "end": v(119.32, -3.29) * mm});
            skArc(sketch, "E9.42.5", {"start": v(112.81, -6.1) * mm, "mid": v(111.49, -7.41) * mm, "end": v(110.9, -9.19) * mm});
            skLineSegment(sketch, "E9.42.6", {"start": v(115.64, -4.88) * mm, "end": v(116.79, -4.6) * mm});
            skLineSegment(sketch, "E9.42.7", {"start": v(114.87, -14.22) * mm, "end": v(115.95, -14.7) * mm});
            skArc(sketch, "E9.43.0", {"start": v(115.48, 7.87) * mm, "mid": v(114.08, 7.21) * mm, "end": v(112.8, 6.36) * mm});
            skArc(sketch, "E9.43.1", {"start": v(112.98, -0.13) * mm, "mid": v(111.72, 1.26) * mm, "end": v(111.24, 3.07) * mm});
            skArc(sketch, "E9.43.2", {"start": v(115.73, -1.5) * mm, "mid": v(114.3, -0.92) * mm, "end": v(112.98, -0.13) * mm});
            skArc(sketch, "E9.43.3", {"start": v(116.86, -1.85) * mm, "mid": v(118.17, -2.43) * mm, "end": v(119.32, -3.29) * mm});
            skArc(sketch, "E9.43.4", {"start": v(116.58, 8.28) * mm, "mid": v(117.86, 8.94) * mm, "end": v(118.96, 9.86) * mm});
            skArc(sketch, "E9.43.5", {"start": v(112.8, 6.36) * mm, "mid": v(111.62, 4.9) * mm, "end": v(111.24, 3.07) * mm});
            skLineSegment(sketch, "E9.43.6", {"start": v(115.48, 7.87) * mm, "end": v(116.58, 8.28) * mm});
            skLineSegment(sketch, "E9.43.7", {"start": v(115.73, -1.5) * mm, "end": v(116.86, -1.85) * mm});
            skArc(sketch, "E9.44.0", {"start": v(113.9, 20.52) * mm, "mid": v(112.6, 19.72) * mm, "end": v(111.42, 18.73) * mm});
            skArc(sketch, "E9.44.1", {"start": v(112.3, 12.3) * mm, "mid": v(110.9, 13.54) * mm, "end": v(110.22, 15.28) * mm});
            skArc(sketch, "E9.44.2", {"start": v(115.2, 11.25) * mm, "mid": v(113.71, 11.66) * mm, "end": v(112.3, 12.3) * mm});
            skArc(sketch, "E9.44.3", {"start": v(116.36, 11.02) * mm, "mid": v(117.72, 10.58) * mm, "end": v(118.96, 9.86) * mm});
            skArc(sketch, "E9.44.4", {"start": v(114.96, 21.06) * mm, "mid": v(116.16, 21.85) * mm, "end": v(117.15, 22.88) * mm});
            skArc(sketch, "E9.44.5", {"start": v(111.42, 18.73) * mm, "mid": v(110.4, 17.15) * mm, "end": v(110.22, 15.28) * mm});
            skLineSegment(sketch, "E9.44.6", {"start": v(113.9, 20.52) * mm, "end": v(114.96, 21.06) * mm});
            skLineSegment(sketch, "E9.44.7", {"start": v(115.2, 11.25) * mm, "end": v(116.36, 11.02) * mm});
            skArc(sketch, "E9.45.0", {"start": v(110.96, 32.93) * mm, "mid": v(109.74, 31.98) * mm, "end": v(108.68, 30.87) * mm});
            skArc(sketch, "E9.45.1", {"start": v(110.27, 24.58) * mm, "mid": v(108.74, 25.66) * mm, "end": v(107.87, 27.32) * mm});
            skArc(sketch, "E9.45.2", {"start": v(113.26, 23.85) * mm, "mid": v(111.74, 24.1) * mm, "end": v(110.27, 24.58) * mm});
            skArc(sketch, "E9.45.3", {"start": v(114.44, 23.75) * mm, "mid": v(115.84, 23.47) * mm, "end": v(117.15, 22.88) * mm});
            skArc(sketch, "E9.45.4", {"start": v(111.95, 33.58) * mm, "mid": v(113.05, 34.5) * mm, "end": v(113.93, 35.63) * mm});
            skArc(sketch, "E9.45.5", {"start": v(108.68, 30.87) * mm, "mid": v(107.85, 29.2) * mm, "end": v(107.87, 27.32) * mm});
            skLineSegment(sketch, "E9.45.6", {"start": v(110.96, 32.93) * mm, "end": v(111.95, 33.58) * mm});
            skLineSegment(sketch, "E9.45.7", {"start": v(113.26, 23.85) * mm, "end": v(114.44, 23.75) * mm});
            skArc(sketch, "E9.46.0", {"start": v(106.66, 44.94) * mm, "mid": v(105.56, 43.86) * mm, "end": v(104.62, 42.64) * mm});
            skArc(sketch, "E9.46.1", {"start": v(106.9, 36.56) * mm, "mid": v(105.26, 37.47) * mm, "end": v(104.21, 39.02) * mm});
            skArc(sketch, "E9.46.2", {"start": v(109.95, 36.16) * mm, "mid": v(108.4, 36.25) * mm, "end": v(106.9, 36.56) * mm});
            skArc(sketch, "E9.46.3", {"start": v(111.13, 36.2) * mm, "mid": v(112.56, 36.07) * mm, "end": v(113.93, 35.63) * mm});
            skArc(sketch, "E9.46.4", {"start": v(107.58, 45.69) * mm, "mid": v(108.57, 46.72) * mm, "end": v(109.31, 47.95) * mm});
            skArc(sketch, "E9.46.5", {"start": v(104.62, 42.64) * mm, "mid": v(103.98, 40.88) * mm, "end": v(104.21, 39.02) * mm});
            skLineSegment(sketch, "E9.46.6", {"start": v(106.66, 44.94) * mm, "end": v(107.58, 45.69) * mm});
            skLineSegment(sketch, "E9.46.7", {"start": v(109.95, 36.16) * mm, "end": v(111.13, 36.2) * mm});
            skArc(sketch, "E9.47.0", {"start": v(101.07, 56.4) * mm, "mid": v(100.1, 55.2) * mm, "end": v(99.3, 53.89) * mm});
            skArc(sketch, "E9.47.1", {"start": v(102.23, 48.1) * mm, "mid": v(100.5, 48.82) * mm, "end": v(99.29, 50.25) * mm});
            skArc(sketch, "E9.47.2", {"start": v(105.3, 48.04) * mm, "mid": v(103.76, 47.95) * mm, "end": v(102.23, 48.1) * mm});
            skArc(sketch, "E9.47.3", {"start": v(106.47, 48.2) * mm, "mid": v(107.9, 48.24) * mm, "end": v(109.31, 47.95) * mm});
            skArc(sketch, "E9.47.4", {"start": v(101.9, 57.25) * mm, "mid": v(102.77, 58.38) * mm, "end": v(103.38, 59.68) * mm});
            skArc(sketch, "E9.47.5", {"start": v(99.3, 53.89) * mm, "mid": v(98.86, 52.07) * mm, "end": v(99.29, 50.25) * mm});
            skLineSegment(sketch, "E9.47.6", {"start": v(101.07, 56.4) * mm, "end": v(101.9, 57.25) * mm});
            skLineSegment(sketch, "E9.47.7", {"start": v(105.3, 48.04) * mm, "end": v(106.47, 48.2) * mm});
            skArc(sketch, "E9.48.0", {"start": v(94.26, 67.17) * mm, "mid": v(93.41, 65.88) * mm, "end": v(92.77, 64.49) * mm});
            skArc(sketch, "E9.48.1", {"start": v(96.32, 59.05) * mm, "mid": v(94.52, 59.58) * mm, "end": v(93.16, 60.86) * mm});
            skArc(sketch, "E9.48.2", {"start": v(99.38, 59.33) * mm, "mid": v(97.86, 59.08) * mm, "end": v(96.32, 59.05) * mm});
            skArc(sketch, "E9.48.3", {"start": v(100.53, 59.62) * mm, "mid": v(101.95, 59.81) * mm, "end": v(103.38, 59.68) * mm});
            skArc(sketch, "E9.48.4", {"start": v(94.98, 68.1) * mm, "mid": v(95.73, 69.33) * mm, "end": v(96.18, 70.7) * mm});
            skArc(sketch, "E9.48.5", {"start": v(92.77, 64.49) * mm, "mid": v(92.53, 62.63) * mm, "end": v(93.16, 60.86) * mm});
            skLineSegment(sketch, "E9.48.6", {"start": v(94.26, 67.17) * mm, "end": v(94.98, 68.1) * mm});
            skLineSegment(sketch, "E9.48.7", {"start": v(99.38, 59.33) * mm, "end": v(100.53, 59.62) * mm});
            skArc(sketch, "E9.49.0", {"start": v(86.3, 77.14) * mm, "mid": v(85.6, 75.76) * mm, "end": v(85.11, 74.3) * mm});
            skArc(sketch, "E9.49.1", {"start": v(89.24, 69.29) * mm, "mid": v(87.4, 69.61) * mm, "end": v(85.9, 70.74) * mm});
            skArc(sketch, "E9.49.2", {"start": v(92.25, 69.9) * mm, "mid": v(90.77, 69.48) * mm, "end": v(89.24, 69.29) * mm});
            skArc(sketch, "E9.49.3", {"start": v(93.36, 70.32) * mm, "mid": v(94.75, 70.67) * mm, "end": v(96.18, 70.7) * mm});
            skArc(sketch, "E9.49.4", {"start": v(86.91, 78.14) * mm, "mid": v(87.52, 79.44) * mm, "end": v(87.82, 80.85) * mm});
            skArc(sketch, "E9.49.5", {"start": v(85.11, 74.3) * mm, "mid": v(85.08, 72.43) * mm, "end": v(85.9, 70.74) * mm});
            skLineSegment(sketch, "E9.49.6", {"start": v(86.3, 77.14) * mm, "end": v(86.91, 78.14) * mm});
            skLineSegment(sketch, "E9.49.7", {"start": v(92.25, 69.9) * mm, "end": v(93.36, 70.32) * mm});
            skArc(sketch, "E9.50.0", {"start": v(77.28, 86.16) * mm, "mid": v(76.74, 84.72) * mm, "end": v(76.42, 83.21) * mm});
            skArc(sketch, "E9.50.1", {"start": v(81.07, 78.68) * mm, "mid": v(79.2, 78.8) * mm, "end": v(77.6, 79.76) * mm});
            skArc(sketch, "E9.50.2", {"start": v(84, 79.63) * mm, "mid": v(82.57, 79.05) * mm, "end": v(81.07, 78.68) * mm});
            skArc(sketch, "E9.50.3", {"start": v(85.05, 80.16) * mm, "mid": v(86.4, 80.66) * mm, "end": v(87.82, 80.85) * mm});
            skArc(sketch, "E9.50.4", {"start": v(77.79, 87.23) * mm, "mid": v(78.25, 88.59) * mm, "end": v(78.4, 90.02) * mm});
            skArc(sketch, "E9.50.5", {"start": v(76.42, 83.21) * mm, "mid": v(76.6, 81.35) * mm, "end": v(77.6, 79.76) * mm});
            skLineSegment(sketch, "E9.50.6", {"start": v(77.28, 86.16) * mm, "end": v(77.79, 87.23) * mm});
            skLineSegment(sketch, "E9.50.7", {"start": v(84, 79.63) * mm, "end": v(85.05, 80.16) * mm});
            skArc(sketch, "E9.51.0", {"start": v(67.34, 94.14) * mm, "mid": v(66.96, 92.65) * mm, "end": v(66.8, 91.11) * mm});
            skArc(sketch, "E9.51.1", {"start": v(71.93, 87.13) * mm, "mid": v(70.05, 87.04) * mm, "end": v(68.35, 87.82) * mm});
            skArc(sketch, "E9.51.2", {"start": v(74.73, 88.39) * mm, "mid": v(73.37, 87.65) * mm, "end": v(71.93, 87.13) * mm});
            skArc(sketch, "E9.51.3", {"start": v(75.72, 89.03) * mm, "mid": v(77, 89.68) * mm, "end": v(78.4, 90.02) * mm});
            skArc(sketch, "E9.51.4", {"start": v(67.72, 95.26) * mm, "mid": v(68.03, 96.66) * mm, "end": v(68.02, 98.1) * mm});
            skArc(sketch, "E9.51.5", {"start": v(66.8, 91.11) * mm, "mid": v(67.18, 89.28) * mm, "end": v(68.35, 87.82) * mm});
            skLineSegment(sketch, "E9.51.6", {"start": v(67.34, 94.14) * mm, "end": v(67.72, 95.26) * mm});
            skLineSegment(sketch, "E9.51.7", {"start": v(74.73, 88.39) * mm, "end": v(75.72, 89.03) * mm});
            skArc(sketch, "E9.52.0", {"start": v(56.57, 100.98) * mm, "mid": v(56.36, 99.45) * mm, "end": v(56.37, 97.9) * mm});
            skArc(sketch, "E9.52.1", {"start": v(61.9, 94.5) * mm, "mid": v(60.05, 94.22) * mm, "end": v(58.27, 94.8) * mm});
            skArc(sketch, "E9.52.2", {"start": v(64.55, 96.07) * mm, "mid": v(63.29, 95.2) * mm, "end": v(61.9, 94.5) * mm});
            skArc(sketch, "E9.52.3", {"start": v(65.47, 96.82) * mm, "mid": v(66.67, 97.6) * mm, "end": v(68.02, 98.1) * mm});
            skArc(sketch, "E9.52.4", {"start": v(56.83, 102.13) * mm, "mid": v(56.98, 103.56) * mm, "end": v(56.81, 104.98) * mm});
            skArc(sketch, "E9.52.5", {"start": v(56.37, 97.9) * mm, "mid": v(56.95, 96.13) * mm, "end": v(58.27, 94.8) * mm});
            skLineSegment(sketch, "E9.52.6", {"start": v(56.57, 100.98) * mm, "end": v(56.83, 102.13) * mm});
            skLineSegment(sketch, "E9.52.7", {"start": v(64.55, 96.07) * mm, "end": v(65.47, 96.82) * mm});
            skArc(sketch, "E9.53.0", {"start": v(45.12, 106.59) * mm, "mid": v(45.08, 105.05) * mm, "end": v(45.26, 103.52) * mm});
            skArc(sketch, "E9.53.1", {"start": v(51.13, 100.75) * mm, "mid": v(49.32, 100.25) * mm, "end": v(47.5, 100.64) * mm});
            skArc(sketch, "E9.53.2", {"start": v(53.6, 102.59) * mm, "mid": v(52.43, 101.58) * mm, "end": v(51.13, 100.75) * mm});
            skArc(sketch, "E9.53.3", {"start": v(54.42, 103.44) * mm, "mid": v(55.53, 104.34) * mm, "end": v(56.81, 104.98) * mm});
            skArc(sketch, "E9.53.4", {"start": v(45.25, 107.76) * mm, "mid": v(45.24, 109.2) * mm, "end": v(44.92, 110.6) * mm});
            skArc(sketch, "E9.53.5", {"start": v(45.26, 103.52) * mm, "mid": v(46.03, 101.8) * mm, "end": v(47.5, 100.64) * mm});
            skLineSegment(sketch, "E9.53.6", {"start": v(45.12, 106.59) * mm, "end": v(45.25, 107.76) * mm});
            skLineSegment(sketch, "E9.53.7", {"start": v(53.6, 102.59) * mm, "end": v(54.42, 103.44) * mm});
            skArc(sketch, "E9.54.0", {"start": v(33.12, 110.9) * mm, "mid": v(33.25, 109.37) * mm, "end": v(33.6, 107.87) * mm});
            skArc(sketch, "E9.54.1", {"start": v(39.74, 105.76) * mm, "mid": v(38, 105.07) * mm, "end": v(36.13, 105.25) * mm});
            skArc(sketch, "E9.54.2", {"start": v(41.98, 107.86) * mm, "mid": v(40.94, 106.73) * mm, "end": v(39.74, 105.76) * mm});
            skArc(sketch, "E9.54.3", {"start": v(42.7, 108.8) * mm, "mid": v(43.71, 109.82) * mm, "end": v(44.92, 110.6) * mm});
            skArc(sketch, "E9.54.4", {"start": v(33.12, 112.09) * mm, "mid": v(32.96, 113.51) * mm, "end": v(32.48, 114.86) * mm});
            skArc(sketch, "E9.54.5", {"start": v(33.6, 107.87) * mm, "mid": v(34.55, 106.25) * mm, "end": v(36.13, 105.25) * mm});
            skLineSegment(sketch, "E9.54.6", {"start": v(33.12, 110.9) * mm, "end": v(33.12, 112.09) * mm});
            skLineSegment(sketch, "E9.54.7", {"start": v(41.98, 107.86) * mm, "end": v(42.7, 108.8) * mm});
            skArc(sketch, "E9.55.0", {"start": v(20.72, 113.87) * mm, "mid": v(21.01, 112.36) * mm, "end": v(21.53, 110.9) * mm});
            skArc(sketch, "E9.55.1", {"start": v(27.86, 109.49) * mm, "mid": v(26.2, 108.61) * mm, "end": v(24.33, 108.59) * mm});
            skArc(sketch, "E9.55.2", {"start": v(29.86, 111.82) * mm, "mid": v(28.95, 110.58) * mm, "end": v(27.86, 109.49) * mm});
            skArc(sketch, "E9.55.3", {"start": v(30.48, 112.83) * mm, "mid": v(31.37, 113.96) * mm, "end": v(32.48, 114.86) * mm});
            skArc(sketch, "E9.55.4", {"start": v(20.59, 115.05) * mm, "mid": v(20.27, 116.45) * mm, "end": v(19.65, 117.74) * mm});
            skArc(sketch, "E9.55.5", {"start": v(21.53, 110.9) * mm, "mid": v(22.65, 109.41) * mm, "end": v(24.33, 108.59) * mm});
            skLineSegment(sketch, "E9.55.6", {"start": v(20.72, 113.87) * mm, "end": v(20.59, 115.05) * mm});
            skLineSegment(sketch, "E9.55.7", {"start": v(29.86, 111.82) * mm, "end": v(30.48, 112.83) * mm});
            skArc(sketch, "E9.56.0", {"start": v(8.07, 115.46) * mm, "mid": v(8.53, 114) * mm, "end": v(9.2, 112.6) * mm});
            skArc(sketch, "E9.56.1", {"start": v(15.65, 111.89) * mm, "mid": v(14.1, 110.84) * mm, "end": v(12.24, 110.6) * mm});
            skArc(sketch, "E9.56.2", {"start": v(17.38, 114.43) * mm, "mid": v(16.6, 113.1) * mm, "end": v(15.65, 111.89) * mm});
            skArc(sketch, "E9.56.3", {"start": v(17.88, 115.5) * mm, "mid": v(18.64, 116.72) * mm, "end": v(19.65, 117.74) * mm});
            skArc(sketch, "E9.56.4", {"start": v(7.8, 116.62) * mm, "mid": v(7.34, 117.97) * mm, "end": v(6.58, 119.19) * mm});
            skArc(sketch, "E9.56.5", {"start": v(9.2, 112.6) * mm, "mid": v(10.48, 111.24) * mm, "end": v(12.24, 110.6) * mm});
            skLineSegment(sketch, "E9.56.6", {"start": v(8.07, 115.46) * mm, "end": v(7.8, 116.62) * mm});
            skLineSegment(sketch, "E9.56.7", {"start": v(17.38, 114.43) * mm, "end": v(17.88, 115.5) * mm});
            skCircle(sketch, "E10", {"center": v(0, 0) * mm, "radius": 108.78 * mm});
            skCircle(sketch, "E11", {"center": v(0, 0) * mm, "radius": 65 * mm});
            skCircle(sketch, "E12", {"center": v(0, 0) * mm, "radius": 117.75 * mm});
            skCircle(sketch, "E13", {"center": v(0, 72) * mm, "radius": 5.25 * mm});
            skCircle(sketch, "E14.1.0", {"center": v(-68.48, 22.25) * mm, "radius": 5.25 * mm});
            skCircle(sketch, "E14.2.0", {"center": v(-42.32, -58.25) * mm, "radius": 5.25 * mm});
            skCircle(sketch, "E14.3.0", {"center": v(42.32, -58.25) * mm, "radius": 5.25 * mm});
            skCircle(sketch, "E14.4.0", {"center": v(68.48, 22.25) * mm, "radius": 5.25 * mm});
            skSolve(sketch);
        }
        {
            var Q0;
            Q0=makeQuery(id+"F0.imprint","IMPRINT",FACE,{"disambiguationData":[TD([[makeQuery(id+"F0.imprint","IMPRINT",EDGE,{"derivedFrom":sQuery(id+"F0.wireOp",EDGE,"E10")}),1.0]])]});
            extrude(context, id + "F1", {"entities" : qUnion([Q0]), "endBound" : BoundingType.SYMMETRIC, "depth" : 4.5 * mm});
        }
        {
            var Q0;
            Q0=makeQuery(id+"F0.imprint","IMPRINT",FACE,{"disambiguationData":[TD([[makeQuery(id+"F0.imprint","IMPRINT",EDGE,{"derivedFrom":sQuery(id+"F0.wireOp",EDGE,"E1")}),-1.0]])]});
            extrude(context, id + "F2", {"entities" : qUnion([Q0]), "operationType" : NewBodyOperationType.ADD, "endBound" : BoundingType.SYMMETRIC, "depth" : 3.16 * mm});
        }
        {
            var Q0;
            Q0=makeQuery(id+"F1.opExtrude","CAP_FACE",FACE,{"disambiguationData":[OSD([sQuery(id+"F0.wireOp",EDGE,"E10"),sQuery(id+"F0.wireOp",EDGE,"E11"),sQuery(id+"F0.wireOp",EDGE,"E13"),sQuery(id+"F0.wireOp",EDGE,"E14.1.0"),sQuery(id+"F0.wireOp",EDGE,"E14.2.0"),sQuery(id+"F0.wireOp",EDGE,"E14.3.0"),sQuery(id+"F0.wireOp",EDGE,"E14.4.0")])],"isStart":false});
            var sketch = newSketch(context, id + "F3", { "sketchPlane" : qUnion([Q0])});
            skArc(sketch, "E15", {"start": v(72.36, -74.28) * mm, "mid": v(77.37, -69.05) * mm, "end": v(82, -63.48) * mm});
            skArc(sketch, "E16", {"start": v(48.9, -50.2) * mm, "mid": v(52.28, -46.66) * mm, "end": v(55.41, -42.9) * mm});
            skLineSegment(sketch, "E17", {"start": v(69.07, 11.87) * mm, "end": v(102.2, 17.56) * mm});
            skLineSegment(sketch, "E18", {"start": v(48.9, -50.2) * mm, "end": v(72.36, -74.28) * mm});
            skLineSegment(sketch, "E19", {"start": v(70.05, 2.14) * mm, "end": v(103.65, 3.17) * mm});
            skLineSegment(sketch, "E20", {"start": v(70.08, 0.3) * mm, "end": v(103.7, 0.45) * mm});
            skLineSegment(sketch, "E21", {"start": v(69.44, -9.45) * mm, "end": v(102.75, -13.98) * mm});
            skLineSegment(sketch, "E22", {"start": v(69.17, -11.26) * mm, "end": v(102.35, -16.67) * mm});
            skLineSegment(sketch, "E23", {"start": v(66.93, -20.78) * mm, "end": v(99.04, -30.75) * mm});
            skLineSegment(sketch, "E24", {"start": v(66.36, -22.53) * mm, "end": v(98.2, -33.33) * mm});
            skLineSegment(sketch, "E25", {"start": v(62.62, -31.47) * mm, "end": v(92.66, -46.57) * mm});
            skLineSegment(sketch, "E26", {"start": v(56.52, -41.44) * mm, "end": v(83.63, -61.32) * mm});
            skLineSegment(sketch, "E27", {"start": v(55.41, -42.9) * mm, "end": v(82, -63.48) * mm});
            skArc(sketch, "E28.trimOffspring", {"start": v(83.63, -61.32) * mm, "mid": v(87.73, -55.28) * mm, "end": v(91.4, -48.98) * mm});
            skArc(sketch, "E29.trimOffspring", {"start": v(56.52, -41.44) * mm, "mid": v(59.3, -37.36) * mm, "end": v(61.77, -33.1) * mm});
            skArc(sketch, "E30.trimOffspring", {"start": v(66.93, -20.78) * mm, "mid": v(68.21, -16.06) * mm, "end": v(69.17, -11.26) * mm});
            skArc(sketch, "E31.trimOffspring", {"start": v(69.44, -9.45) * mm, "mid": v(69.93, -4.58) * mm, "end": v(70.08, 0.3) * mm});
            skArc(sketch, "E32.trimOffspring", {"start": v(70.05, 2.14) * mm, "mid": v(69.73, 7.02) * mm, "end": v(69.07, 11.87) * mm});
            skArc(sketch, "E33.trimOffspring", {"start": v(103.65, 3.17) * mm, "mid": v(103.18, 10.4) * mm, "end": v(102.2, 17.56) * mm});
            skArc(sketch, "E34.trimOffspring", {"start": v(102.75, -13.98) * mm, "mid": v(103.48, -6.78) * mm, "end": v(103.7, 0.45) * mm});
            skArc(sketch, "E35.trimOffspring", {"start": v(99.04, -30.75) * mm, "mid": v(100.94, -23.77) * mm, "end": v(102.35, -16.67) * mm});
            skLineSegment(sketch, "E36", {"start": v(61.77, -33.1) * mm, "end": v(91.4, -48.98) * mm});
            skArc(sketch, "E37.trimOffspring", {"start": v(92.66, -46.57) * mm, "mid": v(95.66, -40.05) * mm, "end": v(98.2, -33.33) * mm});
            skArc(sketch, "E38.trimOffspring", {"start": v(62.62, -31.47) * mm, "mid": v(64.64, -27.06) * mm, "end": v(66.36, -22.53) * mm});
            skLineSegment(sketch, "E39.1.0", {"start": v(50.57, 48.52) * mm, "end": v(74.83, 71.8) * mm});
            skLineSegment(sketch, "E39.1.1", {"start": v(19.6, 67.28) * mm, "end": v(29.02, 99.56) * mm});
            skLineSegment(sketch, "E39.1.2", {"start": v(40.45, 57.23) * mm, "end": v(59.85, 84.69) * mm});
            skLineSegment(sketch, "E39.1.3", {"start": v(10.05, 69.35) * mm, "end": v(14.88, 102.63) * mm});
            skArc(sketch, "E39.1.4", {"start": v(29.02, 99.56) * mm, "mid": v(22, 101.34) * mm, "end": v(14.88, 102.63) * mm});
            skArc(sketch, "E39.1.5", {"start": v(19.6, 67.28) * mm, "mid": v(14.87, 68.48) * mm, "end": v(10.05, 69.35) * mm});
            skArc(sketch, "E39.1.6", {"start": v(40.45, 57.23) * mm, "mid": v(36.35, 59.91) * mm, "end": v(32.09, 62.3) * mm});
            skLineSegment(sketch, "E39.1.7", {"start": v(32.09, 62.3) * mm, "end": v(47.48, 92.2) * mm});
            skLineSegment(sketch, "E39.1.8", {"start": v(30.44, 63.12) * mm, "end": v(45.05, 93.4) * mm});
            skArc(sketch, "E39.1.9", {"start": v(45.05, 93.4) * mm, "mid": v(38.42, 96.32) * mm, "end": v(31.61, 98.76) * mm});
            skLineSegment(sketch, "E39.1.10", {"start": v(21.36, 66.74) * mm, "end": v(31.61, 98.76) * mm});
            skLineSegment(sketch, "E39.1.11", {"start": v(49.28, 49.83) * mm, "end": v(72.92, 73.73) * mm});
            skArc(sketch, "E39.1.12", {"start": v(72.92, 73.73) * mm, "mid": v(67.64, 78.6) * mm, "end": v(62.04, 83.1) * mm});
            skArc(sketch, "E39.1.13", {"start": v(93, 45.86) * mm, "mid": v(89.58, 52.24) * mm, "end": v(85.72, 58.36) * mm});
            skLineSegment(sketch, "E39.1.14", {"start": v(62.85, 31) * mm, "end": v(93, 45.86) * mm});
            skArc(sketch, "E39.1.15", {"start": v(59.85, 84.69) * mm, "mid": v(53.8, 88.66) * mm, "end": v(47.48, 92.2) * mm});
            skArc(sketch, "E39.1.16", {"start": v(56.87, 40.95) * mm, "mid": v(53.85, 44.84) * mm, "end": v(50.57, 48.52) * mm});
            skLineSegment(sketch, "E39.1.17", {"start": v(57.93, 39.44) * mm, "end": v(85.72, 58.36) * mm});
            skArc(sketch, "E39.1.18", {"start": v(30.44, 63.12) * mm, "mid": v(25.97, 65.1) * mm, "end": v(21.36, 66.74) * mm});
            skLineSegment(sketch, "E39.1.19", {"start": v(56.87, 40.95) * mm, "end": v(84.16, 60.59) * mm});
            skLineSegment(sketch, "E39.1.20", {"start": v(41.93, 56.15) * mm, "end": v(62.04, 83.1) * mm});
            skArc(sketch, "E39.1.21", {"start": v(84.16, 60.59) * mm, "mid": v(79.69, 66.36) * mm, "end": v(74.83, 71.8) * mm});
            skArc(sketch, "E39.1.22", {"start": v(49.28, 49.83) * mm, "mid": v(45.71, 53.12) * mm, "end": v(41.93, 56.15) * mm});
            skArc(sketch, "E39.1.23", {"start": v(62.85, 31) * mm, "mid": v(60.54, 35.3) * mm, "end": v(57.93, 39.44) * mm});
            skLineSegment(sketch, "E39.2.0", {"start": v(-30.52, 63.09) * mm, "end": v(-45.16, 93.35) * mm});
            skLineSegment(sketch, "E39.2.1", {"start": v(-57.93, 39.44) * mm, "end": v(-85.72, 58.36) * mm});
            skLineSegment(sketch, "E39.2.2", {"start": v(-41.93, 56.15) * mm, "end": v(-62.05, 83.09) * mm});
            skLineSegment(sketch, "E39.2.3", {"start": v(-62.85, 31) * mm, "end": v(-93, 45.86) * mm});
            skArc(sketch, "E39.2.4", {"start": v(-85.72, 58.36) * mm, "mid": v(-89.58, 52.24) * mm, "end": v(-93, 45.86) * mm});
            skArc(sketch, "E39.2.5", {"start": v(-57.93, 39.44) * mm, "mid": v(-60.54, 35.3) * mm, "end": v(-62.85, 31) * mm});
            skArc(sketch, "E39.2.6", {"start": v(-41.93, 56.15) * mm, "mid": v(-45.75, 53.09) * mm, "end": v(-49.34, 49.77) * mm});
            skLineSegment(sketch, "E39.2.7", {"start": v(-49.34, 49.77) * mm, "end": v(-73, 73.64) * mm});
            skLineSegment(sketch, "E39.2.8", {"start": v(-50.62, 48.46) * mm, "end": v(-74.91, 71.7) * mm});
            skArc(sketch, "E39.2.9", {"start": v(-74.91, 71.7) * mm, "mid": v(-79.73, 66.3) * mm, "end": v(-84.16, 60.58) * mm});
            skLineSegment(sketch, "E39.2.10", {"start": v(-56.88, 40.94) * mm, "end": v(-84.16, 60.58) * mm});
            skLineSegment(sketch, "E39.2.11", {"start": v(-32.16, 62.27) * mm, "end": v(-47.59, 92.14) * mm});
            skArc(sketch, "E39.2.12", {"start": v(-47.59, 92.14) * mm, "mid": v(-53.85, 88.62) * mm, "end": v(-59.85, 84.68) * mm});
            skArc(sketch, "E39.2.13", {"start": v(-14.88, 102.63) * mm, "mid": v(-22, 101.34) * mm, "end": v(-29.02, 99.56) * mm});
            skLineSegment(sketch, "E39.2.14", {"start": v(-10.05, 69.35) * mm, "end": v(-14.88, 102.63) * mm});
            skArc(sketch, "E39.2.15", {"start": v(-62.05, 83.09) * mm, "mid": v(-67.7, 78.56) * mm, "end": v(-73, 73.64) * mm});
            skArc(sketch, "E39.2.16", {"start": v(-21.37, 66.74) * mm, "mid": v(-26, 65.08) * mm, "end": v(-30.52, 63.09) * mm});
            skLineSegment(sketch, "E39.2.17", {"start": v(-19.61, 67.28) * mm, "end": v(-29.02, 99.56) * mm});
            skArc(sketch, "E39.2.18", {"start": v(-50.62, 48.46) * mm, "mid": v(-53.88, 44.81) * mm, "end": v(-56.88, 40.94) * mm});
            skLineSegment(sketch, "E39.2.19", {"start": v(-21.37, 66.74) * mm, "end": v(-31.62, 98.76) * mm});
            skLineSegment(sketch, "E39.2.20", {"start": v(-40.45, 57.23) * mm, "end": v(-59.85, 84.68) * mm});
            skArc(sketch, "E39.2.21", {"start": v(-31.62, 98.76) * mm, "mid": v(-38.48, 96.3) * mm, "end": v(-45.16, 93.35) * mm});
            skArc(sketch, "E39.2.22", {"start": v(-32.16, 62.27) * mm, "mid": v(-36.4, 59.9) * mm, "end": v(-40.45, 57.23) * mm});
            skArc(sketch, "E39.2.23", {"start": v(-10.05, 69.35) * mm, "mid": v(-14.87, 68.48) * mm, "end": v(-19.61, 67.28) * mm});
            skLineSegment(sketch, "E39.3.0", {"start": v(-69.43, -9.53) * mm, "end": v(-102.74, -14.1) * mm});
            skLineSegment(sketch, "E39.3.1", {"start": v(-55.41, -42.9) * mm, "end": v(-82, -63.49) * mm});
            skLineSegment(sketch, "E39.3.2", {"start": v(-66.36, -22.53) * mm, "end": v(-98.2, -33.34) * mm});
            skLineSegment(sketch, "E39.3.3", {"start": v(-48.9, -50.2) * mm, "end": v(-72.36, -74.28) * mm});
            skArc(sketch, "E39.3.4", {"start": v(-82, -63.49) * mm, "mid": v(-77.36, -69.05) * mm, "end": v(-72.36, -74.28) * mm});
            skArc(sketch, "E39.3.5", {"start": v(-55.41, -42.9) * mm, "mid": v(-52.28, -46.67) * mm, "end": v(-48.9, -50.2) * mm});
            skArc(sketch, "E39.3.6", {"start": v(-66.36, -22.53) * mm, "mid": v(-64.63, -27.1) * mm, "end": v(-62.58, -31.54) * mm});
            skLineSegment(sketch, "E39.3.7", {"start": v(-62.58, -31.54) * mm, "end": v(-92.6, -46.68) * mm});
            skLineSegment(sketch, "E39.3.8", {"start": v(-61.73, -33.17) * mm, "end": v(-91.35, -49.08) * mm});
            skArc(sketch, "E39.3.9", {"start": v(-91.35, -49.08) * mm, "mid": v(-87.7, -55.34) * mm, "end": v(-83.63, -61.32) * mm});
            skLineSegment(sketch, "E39.3.10", {"start": v(-56.51, -41.44) * mm, "end": v(-83.63, -61.32) * mm});
            skLineSegment(sketch, "E39.3.11", {"start": v(-69.16, -11.34) * mm, "end": v(-102.33, -16.79) * mm});
            skArc(sketch, "E39.3.12", {"start": v(-102.33, -16.79) * mm, "mid": v(-100.92, -23.83) * mm, "end": v(-99.03, -30.75) * mm});
            skArc(sketch, "E39.3.13", {"start": v(-102.2, 17.56) * mm, "mid": v(-103.18, 10.39) * mm, "end": v(-103.65, 3.16) * mm});
            skLineSegment(sketch, "E39.3.14", {"start": v(-69.07, 11.87) * mm, "end": v(-102.2, 17.56) * mm});
            skArc(sketch, "E39.3.15", {"start": v(-98.2, -33.34) * mm, "mid": v(-95.63, -40.1) * mm, "end": v(-92.6, -46.68) * mm});
            skArc(sketch, "E39.3.16", {"start": v(-70.08, 0.3) * mm, "mid": v(-69.93, -4.62) * mm, "end": v(-69.43, -9.53) * mm});
            skLineSegment(sketch, "E39.3.17", {"start": v(-70.05, 2.14) * mm, "end": v(-103.65, 3.16) * mm});
            skArc(sketch, "E39.3.18", {"start": v(-61.73, -33.17) * mm, "mid": v(-59.27, -37.4) * mm, "end": v(-56.51, -41.44) * mm});
            skLineSegment(sketch, "E39.3.19", {"start": v(-70.08, 0.3) * mm, "end": v(-103.7, 0.45) * mm});
            skLineSegment(sketch, "E39.3.20", {"start": v(-66.93, -20.78) * mm, "end": v(-99.03, -30.75) * mm});
            skArc(sketch, "E39.3.21", {"start": v(-103.7, 0.45) * mm, "mid": v(-103.47, -6.84) * mm, "end": v(-102.74, -14.1) * mm});
            skArc(sketch, "E39.3.22", {"start": v(-69.16, -11.34) * mm, "mid": v(-68.2, -16.1) * mm, "end": v(-66.93, -20.78) * mm});
            skArc(sketch, "E39.3.23", {"start": v(-69.07, 11.87) * mm, "mid": v(-69.73, 7.02) * mm, "end": v(-70.05, 2.14) * mm});
            skSolve(sketch);
        }
        {
            var Q0;
            Q0=makeQuery(id+"F3.imprint","IMPRINT",FACE,{"disambiguationData":[TD([[makeQuery(id+"F3.imprint","IMPRINT",EDGE,{"derivedFrom":sQuery(id+"F3.wireOp",EDGE,"E39.3.1")}),1.0]])]});
            var Q1;
            Q1=makeQuery(id+"F3.imprint","IMPRINT",FACE,{"disambiguationData":[TD([[makeQuery(id+"F3.imprint","IMPRINT",EDGE,{"derivedFrom":sQuery(id+"F3.wireOp",EDGE,"E39.3.8")}),1.0]])]});
            var Q2;
            Q2=makeQuery(id+"F3.imprint","IMPRINT",FACE,{"disambiguationData":[TD([[makeQuery(id+"F3.imprint","IMPRINT",EDGE,{"derivedFrom":sQuery(id+"F3.wireOp",EDGE,"E39.3.2")}),1.0]])]});
            var Q3;
            Q3=makeQuery(id+"F3.imprint","IMPRINT",FACE,{"disambiguationData":[TD([[makeQuery(id+"F3.imprint","IMPRINT",EDGE,{"derivedFrom":sQuery(id+"F3.wireOp",EDGE,"E39.3.13")}),1.0]])]});
            var Q4;
            Q4=makeQuery(id+"F3.imprint","IMPRINT",FACE,{"disambiguationData":[TD([[makeQuery(id+"F3.imprint","IMPRINT",EDGE,{"derivedFrom":sQuery(id+"F3.wireOp",EDGE,"E39.2.1")}),1.0]])]});
            var Q5;
            Q5=makeQuery(id+"F3.imprint","IMPRINT",FACE,{"disambiguationData":[TD([[makeQuery(id+"F3.imprint","IMPRINT",EDGE,{"derivedFrom":sQuery(id+"F3.wireOp",EDGE,"E39.2.8")}),1.0]])]});
            var Q6;
            Q6=makeQuery(id+"F3.imprint","IMPRINT",FACE,{"disambiguationData":[TD([[makeQuery(id+"F3.imprint","IMPRINT",EDGE,{"derivedFrom":sQuery(id+"F3.wireOp",EDGE,"E39.2.2")}),1.0]])]});
            var Q7;
            Q7=makeQuery(id+"F3.imprint","IMPRINT",FACE,{"disambiguationData":[TD([[makeQuery(id+"F3.imprint","IMPRINT",EDGE,{"derivedFrom":sQuery(id+"F3.wireOp",EDGE,"E39.2.13")}),1.0]])]});
            var Q8;
            Q8=makeQuery(id+"F3.imprint","IMPRINT",FACE,{"disambiguationData":[TD([[makeQuery(id+"F3.imprint","IMPRINT",EDGE,{"derivedFrom":sQuery(id+"F3.wireOp",EDGE,"E39.1.1")}),1.0]])]});
            var Q9;
            Q9=makeQuery(id+"F3.imprint","IMPRINT",FACE,{"disambiguationData":[TD([[makeQuery(id+"F3.imprint","IMPRINT",EDGE,{"derivedFrom":sQuery(id+"F3.wireOp",EDGE,"E39.1.8")}),1.0]])]});
            var Q10;
            Q10=makeQuery(id+"F3.imprint","IMPRINT",FACE,{"disambiguationData":[TD([[makeQuery(id+"F3.imprint","IMPRINT",EDGE,{"derivedFrom":sQuery(id+"F3.wireOp",EDGE,"E39.1.2")}),1.0]])]});
            var Q11;
            Q11=makeQuery(id+"F3.imprint","IMPRINT",FACE,{"disambiguationData":[TD([[makeQuery(id+"F3.imprint","IMPRINT",EDGE,{"derivedFrom":sQuery(id+"F3.wireOp",EDGE,"E39.1.13")}),1.0]])]});
            var Q12;
            Q12=makeQuery(id+"F3.imprint","IMPRINT",FACE,{"disambiguationData":[TD([[makeQuery(id+"F3.imprint","IMPRINT",EDGE,{"derivedFrom":sQuery(id+"F3.wireOp",EDGE,"E17")}),-1.0]])]});
            var Q13;
            Q13=makeQuery(id+"F3.imprint","IMPRINT",FACE,{"disambiguationData":[TD([[makeQuery(id+"F3.imprint","IMPRINT",EDGE,{"derivedFrom":sQuery(id+"F3.wireOp",EDGE,"E20")}),-1.0]])]});
            var Q14;
            Q14=makeQuery(id+"F3.imprint","IMPRINT",FACE,{"disambiguationData":[TD([[makeQuery(id+"F3.imprint","IMPRINT",EDGE,{"derivedFrom":sQuery(id+"F3.wireOp",EDGE,"E22")}),-1.0]])]});
            var Q15;
            Q15=makeQuery(id+"F3.imprint","IMPRINT",FACE,{"disambiguationData":[TD([[makeQuery(id+"F3.imprint","IMPRINT",EDGE,{"derivedFrom":sQuery(id+"F3.wireOp",EDGE,"E15")}),1.0]])]});
            extrude(context, id + "F4", {"entities" : qUnion([Q0, Q1, Q2, Q3, Q4, Q5, Q6, Q7, Q8, Q9, Q10, Q11, Q12, Q13, Q14, Q15]), "operationType" : NewBodyOperationType.REMOVE, "oppositeDirection" : true, "depth" : 4.5 * mm});
        }
        {
            var Q0;
            Q0=makeQuery(id+"F3.imprint","IMPRINT",FACE,{"disambiguationData":[TD([[makeQuery(id+"F3.imprint","IMPRINT",EDGE,{"derivedFrom":sQuery(id+"F3.wireOp",EDGE,"E39.3.11")}),1.0]])]});
            var Q1;
            Q1=makeQuery(id+"F3.imprint","IMPRINT",FACE,{"disambiguationData":[TD([[makeQuery(id+"F3.imprint","IMPRINT",EDGE,{"derivedFrom":sQuery(id+"F3.wireOp",EDGE,"E39.3.0")}),-1.0]])]});
            var Q2;
            Q2=makeQuery(id+"F3.imprint","IMPRINT",FACE,{"disambiguationData":[TD([[makeQuery(id+"F3.imprint","IMPRINT",EDGE,{"derivedFrom":sQuery(id+"F3.wireOp",EDGE,"E39.2.11")}),1.0]])]});
            var Q3;
            Q3=makeQuery(id+"F3.imprint","IMPRINT",FACE,{"disambiguationData":[TD([[makeQuery(id+"F3.imprint","IMPRINT",EDGE,{"derivedFrom":sQuery(id+"F3.wireOp",EDGE,"E39.2.0")}),-1.0]])]});
            var Q4;
            Q4=makeQuery(id+"F3.imprint","IMPRINT",FACE,{"disambiguationData":[TD([[makeQuery(id+"F3.imprint","IMPRINT",EDGE,{"derivedFrom":sQuery(id+"F3.wireOp",EDGE,"E39.1.11")}),1.0]])]});
            var Q5;
            Q5=makeQuery(id+"F3.imprint","IMPRINT",FACE,{"disambiguationData":[TD([[makeQuery(id+"F3.imprint","IMPRINT",EDGE,{"derivedFrom":sQuery(id+"F3.wireOp",EDGE,"E39.1.0")}),-1.0]])]});
            var Q6;
            Q6=makeQuery(id+"F3.imprint","IMPRINT",FACE,{"disambiguationData":[TD([[makeQuery(id+"F3.imprint","IMPRINT",EDGE,{"derivedFrom":sQuery(id+"F3.wireOp",EDGE,"E24")}),-1.0]])]});
            var Q7;
            Q7=makeQuery(id+"F3.imprint","IMPRINT",FACE,{"disambiguationData":[TD([[makeQuery(id+"F3.imprint","IMPRINT",EDGE,{"derivedFrom":sQuery(id+"F3.wireOp",EDGE,"E26")}),1.0]])]});
            extrude(context, id + "F5", {"entities" : qUnion([Q0, Q1, Q2, Q3, Q4, Q5, Q6, Q7]), "operationType" : NewBodyOperationType.REMOVE, "oppositeDirection" : true, "depth" : 2 * mm});
        }
        {
            var Q0;
            Q0=makeQuery(id+"F4.boolean.opBoolean","COPY",EDGE,{"derivedFrom":makeQuery(id+"F4.opExtrude","SWEPT_EDGE",EDGE,{"disambiguationData":[OSD([sQuery(id+"F3.wireOp",EDGE,"E39.3.14"),sQuery(id+"F3.wireOp",EDGE,"E39.3.23")])]})});
            var Q1;
            Q1=makeQuery(id+"F4.boolean.opBoolean","COPY",EDGE,{"derivedFrom":makeQuery(id+"F4.opExtrude","SWEPT_EDGE",EDGE,{"disambiguationData":[OSD([sQuery(id+"F3.wireOp",EDGE,"E39.3.17"),sQuery(id+"F3.wireOp",EDGE,"E39.3.23")])]})});
            var Q2;
            Q2=makeQuery(id+"F5.boolean.opBoolean","COPY",EDGE,{"derivedFrom":makeQuery(id+"F5.opExtrude","SWEPT_EDGE",EDGE,{"disambiguationData":[OSD([sQuery(id+"F3.wireOp",EDGE,"E39.3.16"),sQuery(id+"F3.wireOp",EDGE,"E39.3.19")])]})});
            var Q3;
            Q3=makeQuery(id+"F5.boolean.opBoolean","COPY",EDGE,{"derivedFrom":makeQuery(id+"F5.opExtrude","SWEPT_EDGE",EDGE,{"disambiguationData":[OSD([sQuery(id+"F3.wireOp",EDGE,"E39.3.11"),sQuery(id+"F3.wireOp",EDGE,"E39.3.22")])]})});
            var Q4;
            Q4=makeQuery(id+"F4.boolean.opBoolean","COPY",EDGE,{"derivedFrom":makeQuery(id+"F4.opExtrude","SWEPT_EDGE",EDGE,{"disambiguationData":[OSD([sQuery(id+"F3.wireOp",EDGE,"E39.3.2"),sQuery(id+"F3.wireOp",EDGE,"E39.3.6")])]})});
            var Q5;
            Q5=makeQuery(id+"F4.boolean.opBoolean","COPY",EDGE,{"derivedFrom":makeQuery(id+"F4.opExtrude","SWEPT_EDGE",EDGE,{"disambiguationData":[OSD([sQuery(id+"F3.wireOp",EDGE,"E39.3.8"),sQuery(id+"F3.wireOp",EDGE,"E39.3.18")])]})});
            var Q6;
            Q6=makeQuery(id+"F4.boolean.opBoolean","COPY",EDGE,{"derivedFrom":makeQuery(id+"F4.opExtrude","SWEPT_EDGE",EDGE,{"disambiguationData":[OSD([sQuery(id+"F3.wireOp",EDGE,"E39.3.1"),sQuery(id+"F3.wireOp",EDGE,"E39.3.5")])]})});
            var Q7;
            Q7=makeQuery(id+"F4.boolean.opBoolean","COPY",EDGE,{"derivedFrom":makeQuery(id+"F4.opExtrude","SWEPT_EDGE",EDGE,{"disambiguationData":[OSD([sQuery(id+"F3.wireOp",EDGE,"E39.1.1"),sQuery(id+"F3.wireOp",EDGE,"E39.1.4")])]})});
            var Q8;
            Q8=makeQuery(id+"F4.boolean.opBoolean","COPY",EDGE,{"derivedFrom":makeQuery(id+"F4.opExtrude","SWEPT_EDGE",EDGE,{"disambiguationData":[OSD([sQuery(id+"F3.wireOp",EDGE,"E39.1.8"),sQuery(id+"F3.wireOp",EDGE,"E39.1.9")])]})});
            var Q9;
            Q9=makeQuery(id+"F4.boolean.opBoolean","COPY",EDGE,{"derivedFrom":makeQuery(id+"F4.opExtrude","SWEPT_EDGE",EDGE,{"disambiguationData":[OSD([sQuery(id+"F3.wireOp",EDGE,"E39.1.2"),sQuery(id+"F3.wireOp",EDGE,"E39.1.15")])]})});
            var Q10;
            Q10=makeQuery(id+"F5.boolean.opBoolean","COPY",EDGE,{"derivedFrom":makeQuery(id+"F5.opExtrude","SWEPT_EDGE",EDGE,{"disambiguationData":[OSD([sQuery(id+"F3.wireOp",EDGE,"E39.1.11"),sQuery(id+"F3.wireOp",EDGE,"E39.1.12")])]})});
            var Q11;
            Q11=makeQuery(id+"F5.boolean.opBoolean","COPY",EDGE,{"derivedFrom":makeQuery(id+"F5.opExtrude","SWEPT_EDGE",EDGE,{"disambiguationData":[OSD([sQuery(id+"F3.wireOp",EDGE,"E39.3.0"),sQuery(id+"F3.wireOp",EDGE,"E39.3.16")])]})});
            var Q12;
            Q12=makeQuery(id+"F5.boolean.opBoolean","COPY",EDGE,{"derivedFrom":makeQuery(id+"F5.opExtrude","SWEPT_EDGE",EDGE,{"disambiguationData":[OSD([sQuery(id+"F3.wireOp",EDGE,"E39.3.20"),sQuery(id+"F3.wireOp",EDGE,"E39.3.22")])]})});
            var Q13;
            Q13=makeQuery(id+"F4.boolean.opBoolean","COPY",EDGE,{"derivedFrom":makeQuery(id+"F4.opExtrude","SWEPT_EDGE",EDGE,{"disambiguationData":[OSD([sQuery(id+"F3.wireOp",EDGE,"E39.3.6"),sQuery(id+"F3.wireOp",EDGE,"E39.3.7")])]})});
            var Q14;
            Q14=makeQuery(id+"F4.boolean.opBoolean","COPY",EDGE,{"derivedFrom":makeQuery(id+"F4.opExtrude","SWEPT_EDGE",EDGE,{"disambiguationData":[OSD([sQuery(id+"F3.wireOp",EDGE,"E39.3.10"),sQuery(id+"F3.wireOp",EDGE,"E39.3.18")])]})});
            var Q15;
            Q15=makeQuery(id+"F4.boolean.opBoolean","COPY",EDGE,{"derivedFrom":makeQuery(id+"F4.opExtrude","SWEPT_EDGE",EDGE,{"disambiguationData":[OSD([sQuery(id+"F3.wireOp",EDGE,"E39.3.3"),sQuery(id+"F3.wireOp",EDGE,"E39.3.5")])]})});
            var Q16;
            Q16=makeQuery(id+"F4.boolean.opBoolean","COPY",EDGE,{"derivedFrom":makeQuery(id+"F4.opExtrude","SWEPT_EDGE",EDGE,{"disambiguationData":[OSD([sQuery(id+"F3.wireOp",EDGE,"E39.3.13"),sQuery(id+"F3.wireOp",EDGE,"E39.3.14")])]})});
            var Q17;
            Q17=makeQuery(id+"F5.boolean.opBoolean","COPY",EDGE,{"derivedFrom":makeQuery(id+"F5.opExtrude","SWEPT_EDGE",EDGE,{"disambiguationData":[OSD([sQuery(id+"F3.wireOp",EDGE,"E39.3.19"),sQuery(id+"F3.wireOp",EDGE,"E39.3.21")])]})});
            var Q18;
            Q18=makeQuery(id+"F5.boolean.opBoolean","COPY",EDGE,{"derivedFrom":makeQuery(id+"F5.opExtrude","SWEPT_EDGE",EDGE,{"disambiguationData":[OSD([sQuery(id+"F3.wireOp",EDGE,"E39.3.11"),sQuery(id+"F3.wireOp",EDGE,"E39.3.12")])]})});
            var Q19;
            Q19=makeQuery(id+"F4.boolean.opBoolean","COPY",EDGE,{"derivedFrom":makeQuery(id+"F4.opExtrude","SWEPT_EDGE",EDGE,{"disambiguationData":[OSD([sQuery(id+"F3.wireOp",EDGE,"E39.3.2"),sQuery(id+"F3.wireOp",EDGE,"E39.3.15")])]})});
            var Q20;
            Q20=makeQuery(id+"F4.boolean.opBoolean","COPY",EDGE,{"derivedFrom":makeQuery(id+"F4.opExtrude","SWEPT_EDGE",EDGE,{"disambiguationData":[OSD([sQuery(id+"F3.wireOp",EDGE,"E39.3.8"),sQuery(id+"F3.wireOp",EDGE,"E39.3.9")])]})});
            var Q21;
            Q21=makeQuery(id+"F4.boolean.opBoolean","COPY",EDGE,{"derivedFrom":makeQuery(id+"F4.opExtrude","SWEPT_EDGE",EDGE,{"disambiguationData":[OSD([sQuery(id+"F3.wireOp",EDGE,"E39.3.1"),sQuery(id+"F3.wireOp",EDGE,"E39.3.4")])]})});
            var Q22;
            Q22=makeQuery(id+"F4.boolean.opBoolean","COPY",EDGE,{"derivedFrom":makeQuery(id+"F4.opExtrude","SWEPT_EDGE",EDGE,{"disambiguationData":[OSD([sQuery(id+"F3.wireOp",EDGE,"E39.3.13"),sQuery(id+"F3.wireOp",EDGE,"E39.3.17")])]})});
            var Q23;
            Q23=makeQuery(id+"F5.boolean.opBoolean","COPY",EDGE,{"derivedFrom":makeQuery(id+"F5.opExtrude","SWEPT_EDGE",EDGE,{"disambiguationData":[OSD([sQuery(id+"F3.wireOp",EDGE,"E39.3.0"),sQuery(id+"F3.wireOp",EDGE,"E39.3.21")])]})});
            var Q24;
            Q24=makeQuery(id+"F5.boolean.opBoolean","COPY",EDGE,{"derivedFrom":makeQuery(id+"F5.opExtrude","SWEPT_EDGE",EDGE,{"disambiguationData":[OSD([sQuery(id+"F3.wireOp",EDGE,"E39.3.12"),sQuery(id+"F3.wireOp",EDGE,"E39.3.20")])]})});
            var Q25;
            Q25=makeQuery(id+"F4.boolean.opBoolean","COPY",EDGE,{"derivedFrom":makeQuery(id+"F4.opExtrude","SWEPT_EDGE",EDGE,{"disambiguationData":[OSD([sQuery(id+"F3.wireOp",EDGE,"E39.3.7"),sQuery(id+"F3.wireOp",EDGE,"E39.3.15")])]})});
            var Q26;
            Q26=makeQuery(id+"F4.boolean.opBoolean","COPY",EDGE,{"derivedFrom":makeQuery(id+"F4.opExtrude","SWEPT_EDGE",EDGE,{"disambiguationData":[OSD([sQuery(id+"F3.wireOp",EDGE,"E39.3.9"),sQuery(id+"F3.wireOp",EDGE,"E39.3.10")])]})});
            var Q27;
            Q27=makeQuery(id+"F4.boolean.opBoolean","COPY",EDGE,{"derivedFrom":makeQuery(id+"F4.opExtrude","SWEPT_EDGE",EDGE,{"disambiguationData":[OSD([sQuery(id+"F3.wireOp",EDGE,"E39.3.3"),sQuery(id+"F3.wireOp",EDGE,"E39.3.4")])]})});
            var Q28;
            Q28=makeQuery(id+"F5.boolean.opBoolean","COPY",EDGE,{"derivedFrom":makeQuery(id+"F5.opExtrude","SWEPT_EDGE",EDGE,{"disambiguationData":[OSD([sQuery(id+"F3.wireOp",EDGE,"E39.1.0"),sQuery(id+"F3.wireOp",EDGE,"E39.1.21")])]})});
            var Q29;
            Q29=makeQuery(id+"F4.boolean.opBoolean","COPY",EDGE,{"derivedFrom":makeQuery(id+"F4.opExtrude","SWEPT_EDGE",EDGE,{"disambiguationData":[OSD([sQuery(id+"F3.wireOp",EDGE,"E39.1.13"),sQuery(id+"F3.wireOp",EDGE,"E39.1.17")])]})});
            var Q30;
            Q30=makeQuery(id+"F5.boolean.opBoolean","COPY",EDGE,{"derivedFrom":makeQuery(id+"F5.opExtrude","SWEPT_EDGE",EDGE,{"disambiguationData":[OSD([sQuery(id+"F3.wireOp",EDGE,"E39.1.19"),sQuery(id+"F3.wireOp",EDGE,"E39.1.21")])]})});
            var Q31;
            Q31=makeQuery(id+"F4.boolean.opBoolean","COPY",EDGE,{"derivedFrom":makeQuery(id+"F4.opExtrude","SWEPT_EDGE",EDGE,{"disambiguationData":[OSD([sQuery(id+"F3.wireOp",EDGE,"E39.1.13"),sQuery(id+"F3.wireOp",EDGE,"E39.1.14")])]})});
            var Q32;
            Q32=makeQuery(id+"F4.boolean.opBoolean","COPY",EDGE,{"derivedFrom":makeQuery(id+"F4.opExtrude","SWEPT_EDGE",EDGE,{"disambiguationData":[OSD([sQuery(id+"F3.wireOp",EDGE,"E39.1.3"),sQuery(id+"F3.wireOp",EDGE,"E39.1.4")])]})});
            var Q33;
            Q33=makeQuery(id+"F4.boolean.opBoolean","COPY",EDGE,{"derivedFrom":makeQuery(id+"F4.opExtrude","SWEPT_EDGE",EDGE,{"disambiguationData":[OSD([sQuery(id+"F3.wireOp",EDGE,"E39.1.9"),sQuery(id+"F3.wireOp",EDGE,"E39.1.10")])]})});
            var Q34;
            Q34=makeQuery(id+"F4.boolean.opBoolean","COPY",EDGE,{"derivedFrom":makeQuery(id+"F4.opExtrude","SWEPT_EDGE",EDGE,{"disambiguationData":[OSD([sQuery(id+"F3.wireOp",EDGE,"E39.1.7"),sQuery(id+"F3.wireOp",EDGE,"E39.1.15")])]})});
            var Q35;
            Q35=makeQuery(id+"F5.boolean.opBoolean","COPY",EDGE,{"derivedFrom":makeQuery(id+"F5.opExtrude","SWEPT_EDGE",EDGE,{"disambiguationData":[OSD([sQuery(id+"F3.wireOp",EDGE,"E39.1.12"),sQuery(id+"F3.wireOp",EDGE,"E39.1.20")])]})});
            var Q36;
            Q36=makeQuery(id+"F4.boolean.opBoolean","COPY",EDGE,{"derivedFrom":makeQuery(id+"F4.opExtrude","SWEPT_EDGE",EDGE,{"disambiguationData":[OSD([sQuery(id+"F3.wireOp",EDGE,"E39.1.3"),sQuery(id+"F3.wireOp",EDGE,"E39.1.5")])]})});
            var Q37;
            Q37=makeQuery(id+"F4.boolean.opBoolean","COPY",EDGE,{"derivedFrom":makeQuery(id+"F4.opExtrude","SWEPT_EDGE",EDGE,{"disambiguationData":[OSD([sQuery(id+"F3.wireOp",EDGE,"E39.1.10"),sQuery(id+"F3.wireOp",EDGE,"E39.1.18")])]})});
            var Q38;
            Q38=makeQuery(id+"F4.boolean.opBoolean","COPY",EDGE,{"derivedFrom":makeQuery(id+"F4.opExtrude","SWEPT_EDGE",EDGE,{"disambiguationData":[OSD([sQuery(id+"F3.wireOp",EDGE,"E39.1.6"),sQuery(id+"F3.wireOp",EDGE,"E39.1.7")])]})});
            var Q39;
            Q39=makeQuery(id+"F5.boolean.opBoolean","COPY",EDGE,{"derivedFrom":makeQuery(id+"F5.opExtrude","SWEPT_EDGE",EDGE,{"disambiguationData":[OSD([sQuery(id+"F3.wireOp",EDGE,"E39.1.20"),sQuery(id+"F3.wireOp",EDGE,"E39.1.22")])]})});
            var Q40;
            Q40=makeQuery(id+"F5.boolean.opBoolean","COPY",EDGE,{"derivedFrom":makeQuery(id+"F5.opExtrude","SWEPT_EDGE",EDGE,{"disambiguationData":[OSD([sQuery(id+"F3.wireOp",EDGE,"E39.1.0"),sQuery(id+"F3.wireOp",EDGE,"E39.1.16")])]})});
            var Q41;
            Q41=makeQuery(id+"F4.boolean.opBoolean","COPY",EDGE,{"derivedFrom":makeQuery(id+"F4.opExtrude","SWEPT_EDGE",EDGE,{"disambiguationData":[OSD([sQuery(id+"F3.wireOp",EDGE,"E39.1.17"),sQuery(id+"F3.wireOp",EDGE,"E39.1.23")])]})});
            var Q42;
            Q42=makeQuery(id+"F4.boolean.opBoolean","COPY",EDGE,{"derivedFrom":makeQuery(id+"F4.opExtrude","SWEPT_EDGE",EDGE,{"disambiguationData":[OSD([sQuery(id+"F3.wireOp",EDGE,"E39.1.14"),sQuery(id+"F3.wireOp",EDGE,"E39.1.23")])]})});
            var Q43;
            Q43=makeQuery(id+"F5.boolean.opBoolean","COPY",EDGE,{"derivedFrom":makeQuery(id+"F5.opExtrude","SWEPT_EDGE",EDGE,{"disambiguationData":[OSD([sQuery(id+"F3.wireOp",EDGE,"E39.1.16"),sQuery(id+"F3.wireOp",EDGE,"E39.1.19")])]})});
            var Q44;
            Q44=makeQuery(id+"F5.boolean.opBoolean","COPY",EDGE,{"derivedFrom":makeQuery(id+"F5.opExtrude","SWEPT_EDGE",EDGE,{"disambiguationData":[OSD([sQuery(id+"F3.wireOp",EDGE,"E39.1.11"),sQuery(id+"F3.wireOp",EDGE,"E39.1.22")])]})});
            var Q45;
            Q45=makeQuery(id+"F4.boolean.opBoolean","COPY",EDGE,{"derivedFrom":makeQuery(id+"F4.opExtrude","SWEPT_EDGE",EDGE,{"disambiguationData":[OSD([sQuery(id+"F3.wireOp",EDGE,"E39.1.2"),sQuery(id+"F3.wireOp",EDGE,"E39.1.6")])]})});
            var Q46;
            Q46=makeQuery(id+"F4.boolean.opBoolean","COPY",EDGE,{"derivedFrom":makeQuery(id+"F4.opExtrude","SWEPT_EDGE",EDGE,{"disambiguationData":[OSD([sQuery(id+"F3.wireOp",EDGE,"E39.1.1"),sQuery(id+"F3.wireOp",EDGE,"E39.1.5")])]})});
            var Q47;
            Q47=makeQuery(id+"F4.boolean.opBoolean","COPY",EDGE,{"derivedFrom":makeQuery(id+"F4.opExtrude","SWEPT_EDGE",EDGE,{"disambiguationData":[OSD([sQuery(id+"F3.wireOp",EDGE,"E39.1.8"),sQuery(id+"F3.wireOp",EDGE,"E39.1.18")])]})});
            var Q48;
            Q48=makeQuery(id+"F5.boolean.opBoolean","COPY",EDGE,{"derivedFrom":makeQuery(id+"F5.opExtrude","SWEPT_EDGE",EDGE,{"disambiguationData":[OSD([sQuery(id+"F3.wireOp",EDGE,"E39.2.19"),sQuery(id+"F3.wireOp",EDGE,"E39.2.21")])]})});
            var Q49;
            Q49=makeQuery(id+"F4.boolean.opBoolean","COPY",EDGE,{"derivedFrom":makeQuery(id+"F4.opExtrude","SWEPT_EDGE",EDGE,{"disambiguationData":[OSD([sQuery(id+"F3.wireOp",EDGE,"E39.2.13"),sQuery(id+"F3.wireOp",EDGE,"E39.2.14")])]})});
            var Q50;
            Q50=makeQuery(id+"F5.boolean.opBoolean","COPY",EDGE,{"derivedFrom":makeQuery(id+"F5.opExtrude","SWEPT_EDGE",EDGE,{"disambiguationData":[OSD([sQuery(id+"F3.wireOp",EDGE,"E39.2.11"),sQuery(id+"F3.wireOp",EDGE,"E39.2.12")])]})});
            var Q51;
            Q51=makeQuery(id+"F4.boolean.opBoolean","COPY",EDGE,{"derivedFrom":makeQuery(id+"F4.opExtrude","SWEPT_EDGE",EDGE,{"disambiguationData":[OSD([sQuery(id+"F3.wireOp",EDGE,"E39.2.2"),sQuery(id+"F3.wireOp",EDGE,"E39.2.15")])]})});
            var Q52;
            Q52=makeQuery(id+"F4.boolean.opBoolean","COPY",EDGE,{"derivedFrom":makeQuery(id+"F4.opExtrude","SWEPT_EDGE",EDGE,{"disambiguationData":[OSD([sQuery(id+"F3.wireOp",EDGE,"E39.2.8"),sQuery(id+"F3.wireOp",EDGE,"E39.2.9")])]})});
            var Q53;
            Q53=makeQuery(id+"F4.boolean.opBoolean","COPY",EDGE,{"derivedFrom":makeQuery(id+"F4.opExtrude","SWEPT_EDGE",EDGE,{"disambiguationData":[OSD([sQuery(id+"F3.wireOp",EDGE,"E39.2.1"),sQuery(id+"F3.wireOp",EDGE,"E39.2.4")])]})});
            var Q54;
            Q54=makeQuery(id+"F4.boolean.opBoolean","COPY",EDGE,{"derivedFrom":makeQuery(id+"F4.opExtrude","SWEPT_EDGE",EDGE,{"disambiguationData":[OSD([sQuery(id+"F3.wireOp",EDGE,"E39.2.3"),sQuery(id+"F3.wireOp",EDGE,"E39.2.4")])]})});
            var Q55;
            Q55=makeQuery(id+"F4.boolean.opBoolean","COPY",EDGE,{"derivedFrom":makeQuery(id+"F4.opExtrude","SWEPT_EDGE",EDGE,{"disambiguationData":[OSD([sQuery(id+"F3.wireOp",EDGE,"E39.2.7"),sQuery(id+"F3.wireOp",EDGE,"E39.2.15")])]})});
            var Q56;
            Q56=makeQuery(id+"F4.boolean.opBoolean","COPY",EDGE,{"derivedFrom":makeQuery(id+"F4.opExtrude","SWEPT_EDGE",EDGE,{"disambiguationData":[OSD([sQuery(id+"F3.wireOp",EDGE,"E39.2.9"),sQuery(id+"F3.wireOp",EDGE,"E39.2.10")])]})});
            var Q57;
            Q57=makeQuery(id+"F5.boolean.opBoolean","COPY",EDGE,{"derivedFrom":makeQuery(id+"F5.opExtrude","SWEPT_EDGE",EDGE,{"disambiguationData":[OSD([sQuery(id+"F3.wireOp",EDGE,"E39.2.12"),sQuery(id+"F3.wireOp",EDGE,"E39.2.20")])]})});
            var Q58;
            Q58=makeQuery(id+"F5.boolean.opBoolean","COPY",EDGE,{"derivedFrom":makeQuery(id+"F5.opExtrude","SWEPT_EDGE",EDGE,{"disambiguationData":[OSD([sQuery(id+"F3.wireOp",EDGE,"E39.2.0"),sQuery(id+"F3.wireOp",EDGE,"E39.2.21")])]})});
            var Q59;
            Q59=makeQuery(id+"F4.boolean.opBoolean","COPY",EDGE,{"derivedFrom":makeQuery(id+"F4.opExtrude","SWEPT_EDGE",EDGE,{"disambiguationData":[OSD([sQuery(id+"F3.wireOp",EDGE,"E39.2.13"),sQuery(id+"F3.wireOp",EDGE,"E39.2.17")])]})});
            var Q60;
            Q60=makeQuery(id+"F4.boolean.opBoolean","COPY",EDGE,{"derivedFrom":makeQuery(id+"F4.opExtrude","SWEPT_EDGE",EDGE,{"disambiguationData":[OSD([sQuery(id+"F3.wireOp",EDGE,"E39.2.3"),sQuery(id+"F3.wireOp",EDGE,"E39.2.5")])]})});
            var Q61;
            Q61=makeQuery(id+"F4.boolean.opBoolean","COPY",EDGE,{"derivedFrom":makeQuery(id+"F4.opExtrude","SWEPT_EDGE",EDGE,{"disambiguationData":[OSD([sQuery(id+"F3.wireOp",EDGE,"E39.2.10"),sQuery(id+"F3.wireOp",EDGE,"E39.2.18")])]})});
            var Q62;
            Q62=makeQuery(id+"F4.boolean.opBoolean","COPY",EDGE,{"derivedFrom":makeQuery(id+"F4.opExtrude","SWEPT_EDGE",EDGE,{"disambiguationData":[OSD([sQuery(id+"F3.wireOp",EDGE,"E39.2.6"),sQuery(id+"F3.wireOp",EDGE,"E39.2.7")])]})});
            var Q63;
            Q63=makeQuery(id+"F5.boolean.opBoolean","COPY",EDGE,{"derivedFrom":makeQuery(id+"F5.opExtrude","SWEPT_EDGE",EDGE,{"disambiguationData":[OSD([sQuery(id+"F3.wireOp",EDGE,"E39.2.20"),sQuery(id+"F3.wireOp",EDGE,"E39.2.22")])]})});
            var Q64;
            Q64=makeQuery(id+"F5.boolean.opBoolean","COPY",EDGE,{"derivedFrom":makeQuery(id+"F5.opExtrude","SWEPT_EDGE",EDGE,{"disambiguationData":[OSD([sQuery(id+"F3.wireOp",EDGE,"E39.2.0"),sQuery(id+"F3.wireOp",EDGE,"E39.2.16")])]})});
            var Q65;
            Q65=makeQuery(id+"F4.boolean.opBoolean","COPY",EDGE,{"derivedFrom":makeQuery(id+"F4.opExtrude","SWEPT_EDGE",EDGE,{"disambiguationData":[OSD([sQuery(id+"F3.wireOp",EDGE,"E39.2.17"),sQuery(id+"F3.wireOp",EDGE,"E39.2.23")])]})});
            var Q66;
            Q66=makeQuery(id+"F4.boolean.opBoolean","COPY",EDGE,{"derivedFrom":makeQuery(id+"F4.opExtrude","SWEPT_EDGE",EDGE,{"disambiguationData":[OSD([sQuery(id+"F3.wireOp",EDGE,"E39.2.1"),sQuery(id+"F3.wireOp",EDGE,"E39.2.5")])]})});
            var Q67;
            Q67=makeQuery(id+"F4.boolean.opBoolean","COPY",EDGE,{"derivedFrom":makeQuery(id+"F4.opExtrude","SWEPT_EDGE",EDGE,{"disambiguationData":[OSD([sQuery(id+"F3.wireOp",EDGE,"E39.2.8"),sQuery(id+"F3.wireOp",EDGE,"E39.2.18")])]})});
            var Q68;
            Q68=makeQuery(id+"F4.boolean.opBoolean","COPY",EDGE,{"derivedFrom":makeQuery(id+"F4.opExtrude","SWEPT_EDGE",EDGE,{"disambiguationData":[OSD([sQuery(id+"F3.wireOp",EDGE,"E39.2.2"),sQuery(id+"F3.wireOp",EDGE,"E39.2.6")])]})});
            var Q69;
            Q69=makeQuery(id+"F5.boolean.opBoolean","COPY",EDGE,{"derivedFrom":makeQuery(id+"F5.opExtrude","SWEPT_EDGE",EDGE,{"disambiguationData":[OSD([sQuery(id+"F3.wireOp",EDGE,"E39.2.11"),sQuery(id+"F3.wireOp",EDGE,"E39.2.22")])]})});
            var Q70;
            Q70=makeQuery(id+"F5.boolean.opBoolean","COPY",EDGE,{"derivedFrom":makeQuery(id+"F5.opExtrude","SWEPT_EDGE",EDGE,{"disambiguationData":[OSD([sQuery(id+"F3.wireOp",EDGE,"E39.2.16"),sQuery(id+"F3.wireOp",EDGE,"E39.2.19")])]})});
            var Q71;
            Q71=makeQuery(id+"F4.boolean.opBoolean","COPY",EDGE,{"derivedFrom":makeQuery(id+"F4.opExtrude","SWEPT_EDGE",EDGE,{"disambiguationData":[OSD([sQuery(id+"F3.wireOp",EDGE,"E39.2.14"),sQuery(id+"F3.wireOp",EDGE,"E39.2.23")])]})});
            var Q72;
            Q72=makeQuery(id+"F4.boolean.opBoolean","COPY",EDGE,{"derivedFrom":makeQuery(id+"F4.opExtrude","SWEPT_EDGE",EDGE,{"disambiguationData":[OSD([sQuery(id+"F3.wireOp",EDGE,"E16"),sQuery(id+"F3.wireOp",EDGE,"E18")])]})});
            var Q73;
            Q73=makeQuery(id+"F4.boolean.opBoolean","COPY",EDGE,{"derivedFrom":makeQuery(id+"F4.opExtrude","SWEPT_EDGE",EDGE,{"disambiguationData":[OSD([sQuery(id+"F3.wireOp",EDGE,"E16"),sQuery(id+"F3.wireOp",EDGE,"E27")])]})});
            var Q74;
            Q74=makeQuery(id+"F5.boolean.opBoolean","COPY",EDGE,{"derivedFrom":makeQuery(id+"F5.opExtrude","SWEPT_EDGE",EDGE,{"disambiguationData":[OSD([sQuery(id+"F3.wireOp",EDGE,"E29.trimOffspring"),sQuery(id+"F3.wireOp",EDGE,"E36")])]})});
            var Q75;
            Q75=makeQuery(id+"F5.boolean.opBoolean","COPY",EDGE,{"derivedFrom":makeQuery(id+"F5.opExtrude","SWEPT_EDGE",EDGE,{"disambiguationData":[OSD([sQuery(id+"F3.wireOp",EDGE,"E24"),sQuery(id+"F3.wireOp",EDGE,"E38.trimOffspring")])]})});
            var Q76;
            Q76=makeQuery(id+"F4.boolean.opBoolean","COPY",EDGE,{"derivedFrom":makeQuery(id+"F4.opExtrude","SWEPT_EDGE",EDGE,{"disambiguationData":[OSD([sQuery(id+"F3.wireOp",EDGE,"E22"),sQuery(id+"F3.wireOp",EDGE,"E30.trimOffspring")])]})});
            var Q77;
            Q77=makeQuery(id+"F4.boolean.opBoolean","COPY",EDGE,{"derivedFrom":makeQuery(id+"F4.opExtrude","SWEPT_EDGE",EDGE,{"disambiguationData":[OSD([sQuery(id+"F3.wireOp",EDGE,"E20"),sQuery(id+"F3.wireOp",EDGE,"E31.trimOffspring")])]})});
            var Q78;
            Q78=makeQuery(id+"F4.boolean.opBoolean","COPY",EDGE,{"derivedFrom":makeQuery(id+"F4.opExtrude","SWEPT_EDGE",EDGE,{"disambiguationData":[OSD([sQuery(id+"F3.wireOp",EDGE,"E17"),sQuery(id+"F3.wireOp",EDGE,"E32.trimOffspring")])]})});
            var Q79;
            Q79=makeQuery(id+"F5.boolean.opBoolean","COPY",EDGE,{"derivedFrom":makeQuery(id+"F5.opExtrude","SWEPT_EDGE",EDGE,{"disambiguationData":[OSD([sQuery(id+"F3.wireOp",EDGE,"E26"),sQuery(id+"F3.wireOp",EDGE,"E29.trimOffspring")])]})});
            var Q80;
            Q80=makeQuery(id+"F5.boolean.opBoolean","COPY",EDGE,{"derivedFrom":makeQuery(id+"F5.opExtrude","SWEPT_EDGE",EDGE,{"disambiguationData":[OSD([sQuery(id+"F3.wireOp",EDGE,"E25"),sQuery(id+"F3.wireOp",EDGE,"E38.trimOffspring")])]})});
            var Q81;
            Q81=makeQuery(id+"F4.boolean.opBoolean","COPY",EDGE,{"derivedFrom":makeQuery(id+"F4.opExtrude","SWEPT_EDGE",EDGE,{"disambiguationData":[OSD([sQuery(id+"F3.wireOp",EDGE,"E19"),sQuery(id+"F3.wireOp",EDGE,"E32.trimOffspring")])]})});
            var Q82;
            Q82=makeQuery(id+"F4.boolean.opBoolean","COPY",EDGE,{"derivedFrom":makeQuery(id+"F4.opExtrude","SWEPT_EDGE",EDGE,{"disambiguationData":[OSD([sQuery(id+"F3.wireOp",EDGE,"E21"),sQuery(id+"F3.wireOp",EDGE,"E31.trimOffspring")])]})});
            var Q83;
            Q83=makeQuery(id+"F4.boolean.opBoolean","COPY",EDGE,{"derivedFrom":makeQuery(id+"F4.opExtrude","SWEPT_EDGE",EDGE,{"disambiguationData":[OSD([sQuery(id+"F3.wireOp",EDGE,"E23"),sQuery(id+"F3.wireOp",EDGE,"E30.trimOffspring")])]})});
            var Q84;
            Q84=makeQuery(id+"F4.boolean.opBoolean","COPY",EDGE,{"derivedFrom":makeQuery(id+"F4.opExtrude","SWEPT_EDGE",EDGE,{"disambiguationData":[OSD([sQuery(id+"F3.wireOp",EDGE,"E15"),sQuery(id+"F3.wireOp",EDGE,"E27")])]})});
            var Q85;
            Q85=makeQuery(id+"F5.boolean.opBoolean","COPY",EDGE,{"derivedFrom":makeQuery(id+"F5.opExtrude","SWEPT_EDGE",EDGE,{"disambiguationData":[OSD([sQuery(id+"F3.wireOp",EDGE,"E28.trimOffspring"),sQuery(id+"F3.wireOp",EDGE,"E36")])]})});
            var Q86;
            Q86=makeQuery(id+"F5.boolean.opBoolean","COPY",EDGE,{"derivedFrom":makeQuery(id+"F5.opExtrude","SWEPT_EDGE",EDGE,{"disambiguationData":[OSD([sQuery(id+"F3.wireOp",EDGE,"E24"),sQuery(id+"F3.wireOp",EDGE,"E37.trimOffspring")])]})});
            var Q87;
            Q87=makeQuery(id+"F4.boolean.opBoolean","COPY",EDGE,{"derivedFrom":makeQuery(id+"F4.opExtrude","SWEPT_EDGE",EDGE,{"disambiguationData":[OSD([sQuery(id+"F3.wireOp",EDGE,"E20"),sQuery(id+"F3.wireOp",EDGE,"E34.trimOffspring")])]})});
            var Q88;
            Q88=makeQuery(id+"F4.boolean.opBoolean","COPY",EDGE,{"derivedFrom":makeQuery(id+"F4.opExtrude","SWEPT_EDGE",EDGE,{"disambiguationData":[OSD([sQuery(id+"F3.wireOp",EDGE,"E17"),sQuery(id+"F3.wireOp",EDGE,"E33.trimOffspring")])]})});
            var Q89;
            Q89=makeQuery(id+"F4.boolean.opBoolean","COPY",EDGE,{"derivedFrom":makeQuery(id+"F4.opExtrude","SWEPT_EDGE",EDGE,{"disambiguationData":[OSD([sQuery(id+"F3.wireOp",EDGE,"E22"),sQuery(id+"F3.wireOp",EDGE,"E35.trimOffspring")])]})});
            var Q90;
            Q90=makeQuery(id+"F4.boolean.opBoolean","COPY",EDGE,{"derivedFrom":makeQuery(id+"F4.opExtrude","SWEPT_EDGE",EDGE,{"disambiguationData":[OSD([sQuery(id+"F3.wireOp",EDGE,"E19"),sQuery(id+"F3.wireOp",EDGE,"E33.trimOffspring")])]})});
            var Q91;
            Q91=makeQuery(id+"F4.boolean.opBoolean","COPY",EDGE,{"derivedFrom":makeQuery(id+"F4.opExtrude","SWEPT_EDGE",EDGE,{"disambiguationData":[OSD([sQuery(id+"F3.wireOp",EDGE,"E21"),sQuery(id+"F3.wireOp",EDGE,"E34.trimOffspring")])]})});
            var Q92;
            Q92=makeQuery(id+"F4.boolean.opBoolean","COPY",EDGE,{"derivedFrom":makeQuery(id+"F4.opExtrude","SWEPT_EDGE",EDGE,{"disambiguationData":[OSD([sQuery(id+"F3.wireOp",EDGE,"E23"),sQuery(id+"F3.wireOp",EDGE,"E35.trimOffspring")])]})});
            var Q93;
            Q93=makeQuery(id+"F5.boolean.opBoolean","COPY",EDGE,{"derivedFrom":makeQuery(id+"F5.opExtrude","SWEPT_EDGE",EDGE,{"disambiguationData":[OSD([sQuery(id+"F3.wireOp",EDGE,"E25"),sQuery(id+"F3.wireOp",EDGE,"E37.trimOffspring")])]})});
            var Q94;
            Q94=makeQuery(id+"F5.boolean.opBoolean","COPY",EDGE,{"derivedFrom":makeQuery(id+"F5.opExtrude","SWEPT_EDGE",EDGE,{"disambiguationData":[OSD([sQuery(id+"F3.wireOp",EDGE,"E26"),sQuery(id+"F3.wireOp",EDGE,"E28.trimOffspring")])]})});
            var Q95;
            Q95=makeQuery(id+"F4.boolean.opBoolean","COPY",EDGE,{"derivedFrom":makeQuery(id+"F4.opExtrude","SWEPT_EDGE",EDGE,{"disambiguationData":[OSD([sQuery(id+"F3.wireOp",EDGE,"E15"),sQuery(id+"F3.wireOp",EDGE,"E18")])]})});
            fillet(context, id + "F6", {"entities" : qUnion([Q0, Q1, Q2, Q3, Q4, Q5, Q6, Q7, Q8, Q9, Q10, Q11, Q12, Q13, Q14, Q15, Q16, Q17, Q18, Q19, Q20, Q21, Q22, Q23, Q24, Q25, Q26, Q27, Q28, Q29, Q30, Q31, Q32, Q33, Q34, Q35, Q36, Q37, Q38, Q39, Q40, Q41, Q42, Q43, Q44, Q45, Q46, Q47, Q48, Q49, Q50, Q51, Q52, Q53, Q54, Q55, Q56, Q57, Q58, Q59, Q60, Q61, Q62, Q63, Q64, Q65, Q66, Q67, Q68, Q69, Q70, Q71, Q72, Q73, Q74, Q75, Q76, Q77, Q78, Q79, Q80, Q81, Q82, Q83, Q84, Q85, Q86, Q87, Q88, Q89, Q90, Q91, Q92, Q93, Q94, Q95]), "radius" : 2 * mm, "tangentPropagation" : true, "allowEdgeOverflow" : false});
        }
    });
